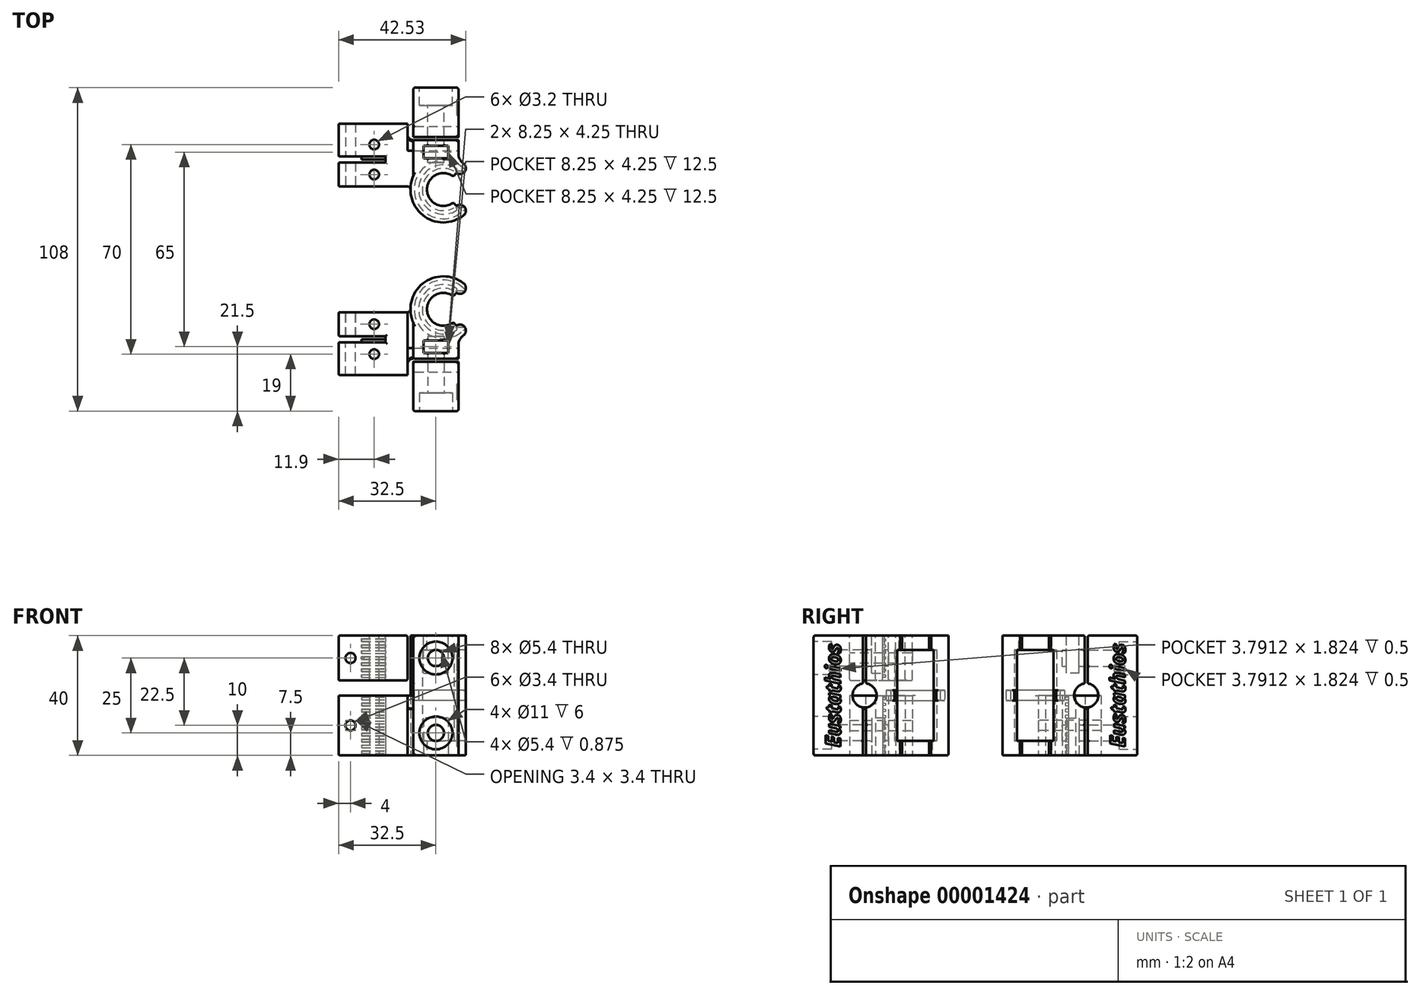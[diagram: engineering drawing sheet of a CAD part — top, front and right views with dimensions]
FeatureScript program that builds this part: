
annotation { "Feature Type Name" : "Feature", "Feature Type Description" : "" }
export const myFeature = defineFeature(function(context is Context, id is Id, definition is map)
    precondition{}
    {
        {
            var Q0;
            Q0=qCreatedBy(makeId("Top.planeOp"),FACE);
            var sketch = newSketch(context, id + "F0", { "sketchPlane" : qUnion([Q0])});
            skArc(sketch, "E0", {"start": v(5, -9.8) * mm, "mid": v(3.61, 10.39) * mm, "end": v(-10, -4.58) * mm});
            skLineSegment(sketch, "E1", {"start": v(5, -34) * mm, "end": v(5, -9.8) * mm});
            skLineSegment(sketch, "E2", {"start": v(-10, -4.58) * mm, "end": v(-10, -34) * mm});
            skLineSegment(sketch, "E3", {"start": v(-10, -34) * mm, "end": v(5, -34) * mm});
            skLineSegment(sketch, "E4", {"start": v(-10, -17) * mm, "end": v(5, -17) * mm, "construction": true});
            skSolve(sketch);
        }
        {
            var Q0;
            Q0 = qSketchRegion(id + "F0", true);
            extrude(context, id + "F1", {"entities" : qUnion([Q0]), "depth" : 40 * mm});
        }
        {
            var Q0;
            Q0=makeQuery(id+"F1.opExtrude","CAP_FACE",FACE,{"disambiguationData":[OSD([sQuery(id+"F0.wireOp",EDGE,"E0"),sQuery(id+"F0.wireOp",EDGE,"E1"),sQuery(id+"F0.wireOp",EDGE,"E2"),sQuery(id+"F0.wireOp",EDGE,"E3")])],"isStart":true});
            var Q1;
            Q1=makeQuery(id+"F1.opExtrude","CAP_FACE",FACE,{"disambiguationData":[OSD([sQuery(id+"F0.wireOp",EDGE,"E0"),sQuery(id+"F0.wireOp",EDGE,"E1"),sQuery(id+"F0.wireOp",EDGE,"E2"),sQuery(id+"F0.wireOp",EDGE,"E3")])],"isStart":false});
            cPlane(context, id + "F2", {"entities" : qUnion([Q0, Q1]), "cplaneType" : CPlaneType.MID_PLANE, "offset" : 150 * mm, "width" : 150 * mm, "height" : 150 * mm});
        }
        {
            var Q0;
            Q0=makeQuery(id+"F1.opExtrude","CAP_FACE",FACE,{"disambiguationData":[OSD([sQuery(id+"F0.wireOp",EDGE,"E0"),sQuery(id+"F0.wireOp",EDGE,"E1"),sQuery(id+"F0.wireOp",EDGE,"E2"),sQuery(id+"F0.wireOp",EDGE,"E3")])],"isStart":true});
            var sketch = newSketch(context, id + "F3", { "sketchPlane" : qUnion([Q0])});
            skLineSegment(sketch, "E5", {"start": v(-35, 1) * mm, "end": v(-35, 9) * mm});
            skLineSegment(sketch, "E6", {"start": v(-35, 9) * mm, "end": v(-19.3, 9) * mm});
            skLineSegment(sketch, "E7", {"start": v(-19.3, 9) * mm, "end": v(-19.3, 11) * mm});
            skLineSegment(sketch, "E8", {"start": v(-19.3, 11) * mm, "end": v(-35, 11) * mm});
            skLineSegment(sketch, "E9", {"start": v(-35, 11) * mm, "end": v(-35, 22) * mm});
            skLineSegment(sketch, "E10", {"start": v(-35, 22) * mm, "end": v(-10, 22) * mm});
            skLineSegment(sketch, "E11", {"start": v(-10, 22) * mm, "end": v(-10, 4.58) * mm});
            skArc(sketch, "E12", {"start": v(-10, 4.58) * mm, "mid": v(-10.75, 2.35) * mm, "end": v(-11, 0) * mm});
            skLineSegment(sketch, "E13", {"start": v(-35, 11) * mm, "end": v(-35, 9) * mm, "construction": true});
            skLineSegment(sketch, "E14", {"start": v(-35, 10) * mm, "end": v(-19.3, 10) * mm, "construction": true});
            skLineSegment(sketch, "E15", {"start": v(-35, 1) * mm, "end": v(-12, 1) * mm});
            skArc(sketch, "E16", {"start": v(-12, 1) * mm, "mid": v(-11.3, 0.7) * mm, "end": v(-11, 0) * mm});
            skSolve(sketch);
        }
        {
            var Q0;
            Q0 = qSketchRegion(id + "F3", true);
            var Q1;
            Q1=qCreatedBy(id+"F2.planeOp",FACE);
            extrude(context, id + "F4", {"entities" : qUnion([Q0]), "operationType" : NewBodyOperationType.ADD, "endBound" : BoundingType.UP_TO_SURFACE, "oppositeDirection" : true, "endBoundEntityFace" : qUnion([Q1]), "depth" : 21 * mm});
        }
        {
            var Q0;
            Q0=makeQuery(id+"F1.opExtrude","SWEPT_FACE",FACE,{"disambiguationData":[OSD([sQuery(id+"F0.wireOp",EDGE,"E1")])]});
            var sketch = newSketch(context, id + "F5", { "sketchPlane" : qUnion([Q0])});
            skLineSegment(sketch, "E17", {"start": v(0, 0) * mm, "end": v(0, 40) * mm, "construction": true});
            skLineSegment(sketch, "E18.0", {"start": v(-9.8, 40) * mm, "end": v(11, 40) * mm, "construction": true});
            skLineSegment(sketch, "E19", {"start": v(0, 20) * mm, "end": v(-17, 20) * mm, "construction": true});
            skPoint(sketch, "E19.endSnap0", {"position": v(0, 20) * mm});
            skLineSegment(sketch, "E20", {"start": v(-17, 20) * mm, "end": v(-34, 20) * mm, "construction": true});
            skCircle(sketch, "E21", {"center": v(-17, 20) * mm, "radius": 4.03 * mm});
            skSolve(sketch);
        }
        {
            var Q0;
            Q0 = qSketchRegion(id + "F5", true);
            var Q1;
            Q1=makeQuery(id+"F1.opExtrude","SWEPT_FACE",FACE,{"disambiguationData":[OSD([sQuery(id+"F0.wireOp",EDGE,"E2")])]});
            extrude(context, id + "F6", {"entities" : qUnion([Q0]), "operationType" : NewBodyOperationType.REMOVE, "oppositeDirection" : true, "endBoundEntityFace" : qUnion([Q1]), "depth" : 17 * mm});
        }
        {
            var Q0;
            Q0=makeQuery(id+"F4.boolean.opBoolean","MERGE",FACE,{"derivedFrom":[makeQuery(id+"F1.opExtrude","CAP_FACE",FACE,{"disambiguationData":[OSD([sQuery(id+"F0.wireOp",EDGE,"E0"),sQuery(id+"F0.wireOp",EDGE,"E1"),sQuery(id+"F0.wireOp",EDGE,"E2"),sQuery(id+"F0.wireOp",EDGE,"E3")])],"isStart":true}),makeQuery(id+"F4.opExtrude","CAP_FACE",FACE,{"disambiguationData":[OSD([sQuery(id+"F3.wireOp",EDGE,"E5"),sQuery(id+"F3.wireOp",EDGE,"E6"),sQuery(id+"F3.wireOp",EDGE,"E7"),sQuery(id+"F3.wireOp",EDGE,"E8"),sQuery(id+"F3.wireOp",EDGE,"E9"),sQuery(id+"F3.wireOp",EDGE,"E10"),sQuery(id+"F3.wireOp",EDGE,"E11"),sQuery(id+"F3.wireOp",EDGE,"E12"),sQuery(id+"F3.wireOp",EDGE,"E15"),sQuery(id+"F3.wireOp",EDGE,"E16")])],"isStart":true})]});
            var sketch = newSketch(context, id + "F7", { "sketchPlane" : qUnion([Q0])});
            skLineSegment(sketch, "E22.0", {"start": v(-12, 12.98) * mm, "end": v(-10, 12.98) * mm, "construction": true});
            skLineSegment(sketch, "E23.0", {"start": v(-12, 12.97) * mm, "end": v(-12, 12.97) * mm});
            skLineSegment(sketch, "E24", {"start": v(-10, 17.5) * mm, "end": v(5, 17.5) * mm});
            skLineSegment(sketch, "E25", {"start": v(5, 17.5) * mm, "end": v(5, 16.5) * mm});
            skLineSegment(sketch, "E26", {"start": v(5, 17) * mm, "end": v(-12, 17) * mm, "construction": true});
            skLineSegment(sketch, "E27", {"start": v(5, 16.5) * mm, "end": v(-10, 16.5) * mm});
            skLineSegment(sketch, "E28.0", {"start": v(-12, 12.97) * mm, "end": v(-12, 21.03) * mm, "construction": true});
            skLineSegment(sketch, "E29", {"start": v(-10, 22) * mm, "end": v(-10, 17.5) * mm});
            skLineSegment(sketch, "E30", {"start": v(-10, 22) * mm, "end": v(-12, 22) * mm});
            skLineSegment(sketch, "E31", {"start": v(-12, 22) * mm, "end": v(-12, 18.5) * mm});
            skPoint(sketch, "E32.visualSharp", {"position": v(-12, 16.5) * mm});
            skArc(sketch, "E32.filletArc", {"start": v(-12, 18.5) * mm, "mid": v(-11.41, 17.09) * mm, "end": v(-10, 16.5) * mm});
            skSolve(sketch);
        }
        {
            var Q0;
            Q0 = qSketchRegion(id + "F7", true);
            extrude(context, id + "F8", {"entities" : qUnion([Q0]), "operationType" : NewBodyOperationType.REMOVE, "endBound" : BoundingType.THROUGH_ALL, "oppositeDirection" : true, "depth" : 25 * mm});
        }
        {
            var Q0;
            {var subQ0=sQuery(id+"F3.wireOp",EDGE,"E10");var subQ1=sQuery(id+"F3.wireOp",EDGE,"E9");var subQ2=sQuery(id+"F3.wireOp",EDGE,"E8");var subQ3=sQuery(id+"F3.wireOp",EDGE,"E7");var subQ4=sQuery(id+"F0.wireOp",EDGE,"E1");var subQ5=sQuery(id+"F0.wireOp",EDGE,"E0");var subQ6=sQuery(id+"F3.wireOp",EDGE,"E16");var subQ7=sQuery(id+"F3.wireOp",EDGE,"E15");var subQ8=sQuery(id+"F3.wireOp",EDGE,"E5");var subQ9=sQuery(id+"F3.wireOp",EDGE,"E6");Q0=makeQuery(id+"F8.boolean.opBoolean","SPLIT",FACE,{"disambiguationData":[TD([makeQuery(id+"F1.opExtrude","SWEPT_FACE",FACE,{"disambiguationData":[OSD([subQ5])]})])],"derivedFrom":makeQuery(id+"F4.boolean.opBoolean","MERGE",FACE,{"derivedFrom":[makeQuery(id+"F1.opExtrude","CAP_FACE",FACE,{"disambiguationData":[OSD([subQ5,subQ4,sQuery(id+"F0.wireOp",EDGE,"E2"),sQuery(id+"F0.wireOp",EDGE,"E3")])],"isStart":true}),makeQuery(id+"F4.opExtrude","CAP_FACE",FACE,{"disambiguationData":[OSD([subQ8,subQ9,subQ3,subQ2,subQ1,subQ0,sQuery(id+"F3.wireOp",EDGE,"E11"),sQuery(id+"F3.wireOp",EDGE,"E12"),subQ7,subQ6])],"isStart":true})]})});}
            var sketch = newSketch(context, id + "F9", { "sketchPlane" : qUnion([Q0])});
            skCircle(sketch, "E33", {"center": v(0, 0) * mm, "radius": 7.05 * mm});
            skSolve(sketch);
        }
        {
            var Q0;
            Q0 = qSketchRegion(id + "F9", true);
            extrude(context, id + "F10", {"entities" : qUnion([Q0]), "operationType" : NewBodyOperationType.REMOVE, "endBound" : BoundingType.THROUGH_ALL, "oppositeDirection" : true, "depth" : 25 * mm});
        }
        {
            var Q0;
            {var subQ0=sQuery(id+"F3.wireOp",EDGE,"E10");var subQ1=sQuery(id+"F3.wireOp",EDGE,"E9");var subQ2=sQuery(id+"F3.wireOp",EDGE,"E8");var subQ3=sQuery(id+"F3.wireOp",EDGE,"E7");var subQ4=sQuery(id+"F0.wireOp",EDGE,"E1");var subQ5=sQuery(id+"F0.wireOp",EDGE,"E0");var subQ6=sQuery(id+"F3.wireOp",EDGE,"E16");var subQ7=sQuery(id+"F3.wireOp",EDGE,"E15");var subQ8=sQuery(id+"F3.wireOp",EDGE,"E5");var subQ9=sQuery(id+"F3.wireOp",EDGE,"E6");Q0=makeQuery(id+"F8.boolean.opBoolean","SPLIT",FACE,{"disambiguationData":[TD([makeQuery(id+"F1.opExtrude","SWEPT_FACE",FACE,{"disambiguationData":[OSD([subQ5])]})])],"derivedFrom":makeQuery(id+"F4.boolean.opBoolean","MERGE",FACE,{"derivedFrom":[makeQuery(id+"F1.opExtrude","CAP_FACE",FACE,{"disambiguationData":[OSD([subQ5,subQ4,sQuery(id+"F0.wireOp",EDGE,"E2"),sQuery(id+"F0.wireOp",EDGE,"E3")])],"isStart":true}),makeQuery(id+"F4.opExtrude","CAP_FACE",FACE,{"disambiguationData":[OSD([subQ8,subQ9,subQ3,subQ2,subQ1,subQ0,sQuery(id+"F3.wireOp",EDGE,"E11"),sQuery(id+"F3.wireOp",EDGE,"E12"),subQ7,subQ6])],"isStart":true})]})});}
            var sketch = newSketch(context, id + "F11", { "sketchPlane" : qUnion([Q0])});
            skLineSegment(sketch, "E34", {"start": v(0, 0) * mm, "end": v(8.5, 6.98) * mm, "construction": true});
            skLineSegment(sketch, "E35", {"start": v(8.5, -6.98) * mm, "end": v(0, 0) * mm, "construction": true});
            skArc(sketch, "E36", {"start": v(6.77, -8.67) * mm, "mid": v(7.11, -5.9) * mm, "end": v(4.34, -5.56) * mm});
            skLineSegment(sketch, "E37", {"start": v(0, 0) * mm, "end": v(14.65, 0) * mm, "construction": true});
            skArc(sketch, "E38", {"start": v(4.34, 5.56) * mm, "mid": v(7.11, 5.9) * mm, "end": v(6.77, 8.67) * mm});
            skLineSegment(sketch, "E39", {"start": v(5.56, 7.11) * mm, "end": v(0, 0) * mm, "construction": true});
            skLineSegment(sketch, "E40", {"start": v(0, 0) * mm, "end": v(5.56, -7.11) * mm, "construction": true});
            skArc(sketch, "E41", {"start": v(4.34, 5.56) * mm, "mid": v(7.05, 0) * mm, "end": v(4.34, -5.56) * mm});
            skSolve(sketch);
        }
        {
            var Q0;
            Q0 = qSketchRegion(id + "F11", true);
            var Q1;
            {var subQ2=sQuery(id+"F11.wireOp",EDGE,"E36");Q1=makeQuery(id+"F11.imprint","IMPRINT",FACE,{"disambiguationData":[TD([[makeQuery(id+"F11.imprint","IMPRINT",EDGE,{"derivedFrom":subQ2}),-1.0]])]});}
            extrude(context, id + "F12", {"entities" : qUnion([Q0, Q1]), "operationType" : NewBodyOperationType.REMOVE, "endBound" : BoundingType.THROUGH_ALL, "oppositeDirection" : true, "depth" : 25 * mm});
        }
        {
            var Q0;
            Q0=makeQuery(id+"F1.opExtrude","SWEPT_EDGE",EDGE,{"disambiguationData":[OSD([sQuery(id+"F0.wireOp",EDGE,"E0"),sQuery(id+"F0.wireOp",EDGE,"E1")])]});
            fillet(context, id + "F13", {"entities" : qUnion([Q0]), "radius" : 4 * mm, "tangentPropagation" : true, "allowEdgeOverflow" : false});
        }
        {
            var Q0;
            Q0=qCreatedBy(makeId("Right.planeOp"),FACE);
            var sketch = newSketch(context, id + "F14", { "sketchPlane" : qUnion([Q0])});
            skLineSegment(sketch, "E42.rect.bottom", {"start": v(-6.1, 35.2) * mm, "end": v(6.1, 35.2) * mm});
            skLineSegment(sketch, "E42.rect.top", {"start": v(-6.1, 4.8) * mm, "end": v(6.1, 4.8) * mm});
            skLineSegment(sketch, "E42.rect.left", {"start": v(-6.1, 35.2) * mm, "end": v(-6.1, 4.8) * mm});
            skLineSegment(sketch, "E42.rect.right", {"start": v(6.1, 35.2) * mm, "end": v(6.1, 4.8) * mm});
            skPoint(sketch, "E42.rect.middle", {"position": v(0, 20) * mm});
            skLineSegment(sketch, "E43", {"start": v(-5.14, 40) * mm, "end": v(-5.14, 0) * mm, "construction": true});
            skLineSegment(sketch, "E44", {"start": v(5.14, 0) * mm, "end": v(5.14, 40) * mm, "construction": true});
            skLineSegment(sketch, "E45", {"start": v(-5.14, 0) * mm, "end": v(5.14, 0) * mm, "construction": true});
            skLineSegment(sketch, "E46", {"start": v(-5.14, 40) * mm, "end": v(5.14, 40) * mm, "construction": true});
            skLineSegment(sketch, "E47", {"start": v(0, 0) * mm, "end": v(0, 40) * mm, "construction": true});
            skSolve(sketch);
        }
        {
            var Q0;
            Q0 = qSketchRegion(id + "F14", true);
            extrude(context, id + "F15", {"entities" : qUnion([Q0]), "operationType" : NewBodyOperationType.REMOVE, "endBound" : BoundingType.THROUGH_ALL, "depth" : 25 * mm});
        }
        {
            var Q0;
            {var subQ0=sQuery(id+"F3.wireOp",EDGE,"E10");var subQ1=sQuery(id+"F3.wireOp",EDGE,"E9");var subQ2=sQuery(id+"F3.wireOp",EDGE,"E8");var subQ3=sQuery(id+"F3.wireOp",EDGE,"E7");var subQ4=sQuery(id+"F0.wireOp",EDGE,"E1");var subQ5=sQuery(id+"F0.wireOp",EDGE,"E0");var subQ6=sQuery(id+"F3.wireOp",EDGE,"E16");var subQ7=sQuery(id+"F3.wireOp",EDGE,"E15");var subQ8=sQuery(id+"F3.wireOp",EDGE,"E5");var subQ9=sQuery(id+"F3.wireOp",EDGE,"E6");Q0=makeQuery(id+"F8.boolean.opBoolean","SPLIT",FACE,{"disambiguationData":[TD([makeQuery(id+"F1.opExtrude","SWEPT_FACE",FACE,{"disambiguationData":[OSD([subQ5])]})])],"derivedFrom":makeQuery(id+"F4.boolean.opBoolean","MERGE",FACE,{"derivedFrom":[makeQuery(id+"F1.opExtrude","CAP_FACE",FACE,{"disambiguationData":[OSD([subQ5,subQ4,sQuery(id+"F0.wireOp",EDGE,"E2"),sQuery(id+"F0.wireOp",EDGE,"E3")])],"isStart":true}),makeQuery(id+"F4.opExtrude","CAP_FACE",FACE,{"disambiguationData":[OSD([subQ8,subQ9,subQ3,subQ2,subQ1,subQ0,sQuery(id+"F3.wireOp",EDGE,"E11"),sQuery(id+"F3.wireOp",EDGE,"E12"),subQ7,subQ6])],"isStart":true})]})});}
            var sketch = newSketch(context, id + "F16", { "sketchPlane" : qUnion([Q0])});
            skArc(sketch, "E48", {"start": v(3.39, 4.33) * mm, "mid": v(-5.5, 0) * mm, "end": v(3.39, -4.33) * mm});
            skArc(sketch, "E49.0", {"start": v(4.34, 5.56) * mm, "mid": v(-7.05, 0) * mm, "end": v(4.34, -5.56) * mm});
            skLineSegment(sketch, "E50", {"start": v(0, 0) * mm, "end": v(6.8, 5.58) * mm, "construction": true});
            skLineSegment(sketch, "E51", {"start": v(0, 0) * mm, "end": v(6.8, -5.58) * mm, "construction": true});
            skArc(sketch, "E52", {"start": v(4.34, 5.56) * mm, "mid": v(5.58, 5.14) * mm, "end": v(6.8, 5.58) * mm});
            skArc(sketch, "E53", {"start": v(4.34, -5.56) * mm, "mid": v(5.58, -5.14) * mm, "end": v(6.8, -5.58) * mm});
            skLineSegment(sketch, "E54", {"start": v(4.34, 5.56) * mm, "end": v(3.39, 4.33) * mm});
            skLineSegment(sketch, "E55", {"start": v(3.39, -4.33) * mm, "end": v(4.34, -5.56) * mm});
            skLineSegment(sketch, "E56", {"start": v(3.39, 4.33) * mm, "end": v(0, 0) * mm, "construction": true});
            skLineSegment(sketch, "E57", {"start": v(3.39, -4.33) * mm, "end": v(0, 0) * mm, "construction": true});
            skSolve(sketch);
        }
        {
            var Q0;
            Q0 = qSketchRegion(id + "F16", true);
            var Q1;
            Q1=makeQuery(id+"F15.boolean.opBoolean","COPY",FACE,{"disambiguationData":[OD(0.0)],"derivedFrom":makeQuery(id+"F15.opExtrude","SWEPT_FACE",FACE,{"disambiguationData":[OSD([sQuery(id+"F14.wireOp",EDGE,"E42.rect.top")])]})});
            extrude(context, id + "F17", {"entities" : qUnion([Q0]), "operationType" : NewBodyOperationType.ADD, "endBound" : BoundingType.UP_TO_SURFACE, "oppositeDirection" : true, "endBoundEntityFace" : qUnion([Q1]), "depth" : 2.4 * mm});
        }
        {
            var Q0;
            {var subQ0=sQuery(id+"F0.wireOp",EDGE,"E0");var subQ1=sQuery(id+"F0.wireOp",EDGE,"E1");var subQ2=sQuery(id+"F0.wireOp",EDGE,"E2");Q0=makeQuery(id+"F8.boolean.opBoolean","SPLIT",FACE,{"disambiguationData":[TD([makeQuery(id+"F1.opExtrude","SWEPT_FACE",FACE,{"disambiguationData":[OSD([subQ0])]})])],"derivedFrom":makeQuery(id+"F1.opExtrude","CAP_FACE",FACE,{"disambiguationData":[OSD([subQ0,subQ1,subQ2,sQuery(id+"F0.wireOp",EDGE,"E3")])],"isStart":false})});}
            var sketch = newSketch(context, id + "F18", { "sketchPlane" : qUnion([Q0])});
            skArc(sketch, "E58.0", {"start": v(3.39, -4.33) * mm, "mid": v(-5.5, 0) * mm, "end": v(3.39, 4.33) * mm});
            skLineSegment(sketch, "E59.0", {"start": v(4.34, -5.56) * mm, "end": v(3.39, -4.33) * mm});
            skLineSegment(sketch, "E60.0", {"start": v(3.39, 4.33) * mm, "end": v(4.34, 5.56) * mm});
            skArc(sketch, "E61.0", {"start": v(4.34, 5.56) * mm, "mid": v(-7.05, 0) * mm, "end": v(4.34, -5.56) * mm});
            skSolve(sketch);
        }
        {
            var Q0;
            Q0 = qSketchRegion(id + "F18", true);
            var Q1;
            Q1=makeQuery(id+"F15.boolean.opBoolean","COPY",FACE,{"disambiguationData":[OD(0.0)],"derivedFrom":makeQuery(id+"F15.opExtrude","SWEPT_FACE",FACE,{"disambiguationData":[OSD([sQuery(id+"F14.wireOp",EDGE,"E42.rect.bottom")])]})});
            extrude(context, id + "F19", {"entities" : qUnion([Q0]), "operationType" : NewBodyOperationType.ADD, "endBound" : BoundingType.UP_TO_SURFACE, "oppositeDirection" : true, "endBoundEntityFace" : qUnion([Q1]), "depth" : 2.4 * mm});
        }
        {
            var Q0;
            {var subQ0=sQuery(id+"F0.wireOp",EDGE,"E0");var subQ1=sQuery(id+"F0.wireOp",EDGE,"E1");var subQ2=sQuery(id+"F0.wireOp",EDGE,"E2");Q0=makeQuery(id+"F19.boolean.opBoolean","MERGE",FACE,{"derivedFrom":[makeQuery(id+"F8.boolean.opBoolean","SPLIT",FACE,{"disambiguationData":[TD([makeQuery(id+"F1.opExtrude","SWEPT_FACE",FACE,{"disambiguationData":[OSD([subQ0])]})])],"derivedFrom":makeQuery(id+"F1.opExtrude","CAP_FACE",FACE,{"disambiguationData":[OSD([subQ0,subQ1,subQ2,sQuery(id+"F0.wireOp",EDGE,"E3")])],"isStart":false})}),makeQuery(id+"F19.opExtrude","CAP_FACE",FACE,{"disambiguationData":[OSD([sQuery(id+"F18.wireOp",EDGE,"825981b6-10bd-436c-b23c-b1dcfb23399f.0"),sQuery(id+"F18.wireOp",EDGE,"26848335-8289-480a-91f7-f3094b967ab5.0"),sQuery(id+"F18.wireOp",EDGE,"958e6e3c-ce8c-4eca-b8df-495d4845233b.0"),sQuery(id+"F18.wireOp",EDGE,"a21f0ce2-bef5-4404-b2f3-7f19712db0ed.0"),sQuery(id+"F18.wireOp",EDGE,"5b232a10-1d2d-4218-a2a3-206db68530f9.0"),sQuery(id+"F18.wireOp",EDGE,"9355f6d4-eb2a-417f-8d43-74a68f565168.0")])],"isStart":true})]});}
            var sketch = newSketch(context, id + "F20", { "sketchPlane" : qUnion([Q0])});
            skLineSegment(sketch, "E62", {"start": v(-2.5, -16.5) * mm, "end": v(-2.5, -12.5) * mm, "construction": true});
            skLineSegment(sketch, "E63.rect.bottom", {"start": v(-6.62, -14.62) * mm, "end": v(1.63, -14.62) * mm});
            skLineSegment(sketch, "E63.rect.top", {"start": v(-6.62, -10.37) * mm, "end": v(1.63, -10.38) * mm});
            skLineSegment(sketch, "E63.rect.left", {"start": v(-6.62, -14.62) * mm, "end": v(-6.62, -10.37) * mm});
            skLineSegment(sketch, "E63.rect.right", {"start": v(1.63, -14.62) * mm, "end": v(1.63, -10.38) * mm});
            skPoint(sketch, "E63.rect.middle", {"position": v(-2.5, -12.5) * mm});
            skSolve(sketch);
        }
        {
            var Q0;
            Q0 = qSketchRegion(id + "F20", true);
            extrude(context, id + "F21", {"entities" : qUnion([Q0]), "operationType" : NewBodyOperationType.REMOVE, "oppositeDirection" : true, "depth" : 12.5 * mm});
        }
        {
            var Q0;
            {var subQ0=sQuery(id+"F3.wireOp",EDGE,"E10");var subQ1=sQuery(id+"F3.wireOp",EDGE,"E9");var subQ2=sQuery(id+"F3.wireOp",EDGE,"E8");var subQ3=sQuery(id+"F3.wireOp",EDGE,"E7");var subQ4=sQuery(id+"F0.wireOp",EDGE,"E1");var subQ5=sQuery(id+"F0.wireOp",EDGE,"E0");var subQ6=sQuery(id+"F3.wireOp",EDGE,"E16");var subQ7=sQuery(id+"F3.wireOp",EDGE,"E15");var subQ8=sQuery(id+"F3.wireOp",EDGE,"E5");var subQ9=sQuery(id+"F3.wireOp",EDGE,"E6");Q0=makeQuery(id+"F17.boolean.opBoolean","MERGE",FACE,{"derivedFrom":[makeQuery(id+"F8.boolean.opBoolean","SPLIT",FACE,{"disambiguationData":[TD([makeQuery(id+"F1.opExtrude","SWEPT_FACE",FACE,{"disambiguationData":[OSD([subQ5])]})])],"derivedFrom":makeQuery(id+"F4.boolean.opBoolean","MERGE",FACE,{"derivedFrom":[makeQuery(id+"F1.opExtrude","CAP_FACE",FACE,{"disambiguationData":[OSD([subQ5,subQ4,sQuery(id+"F0.wireOp",EDGE,"E2"),sQuery(id+"F0.wireOp",EDGE,"E3")])],"isStart":true}),makeQuery(id+"F4.opExtrude","CAP_FACE",FACE,{"disambiguationData":[OSD([subQ8,subQ9,subQ3,subQ2,subQ1,subQ0,sQuery(id+"F3.wireOp",EDGE,"E11"),sQuery(id+"F3.wireOp",EDGE,"E12"),subQ7,subQ6])],"isStart":true})]})}),makeQuery(id+"F17.opExtrude","CAP_FACE",FACE,{"disambiguationData":[OSD([sQuery(id+"F16.wireOp",EDGE,"E48"),sQuery(id+"F16.wireOp",EDGE,"E49.0"),sQuery(id+"F16.wireOp",EDGE,"E54"),sQuery(id+"F16.wireOp",EDGE,"E55")])],"isStart":true})]});}
            var sketch = newSketch(context, id + "F22", { "sketchPlane" : qUnion([Q0])});
            skLineSegment(sketch, "E64.0.0", {"start": v(-6.62, 10.37) * mm, "end": v(-6.62, 14.62) * mm});
            skLineSegment(sketch, "E64.0.1", {"start": v(-6.62, 14.62) * mm, "end": v(1.63, 14.62) * mm});
            skLineSegment(sketch, "E64.0.2", {"start": v(1.63, 14.62) * mm, "end": v(1.63, 10.38) * mm});
            skLineSegment(sketch, "E64.0.3", {"start": v(1.63, 10.38) * mm, "end": v(-6.62, 10.37) * mm});
            skSolve(sketch);
        }
        {
            var Q0;
            Q0 = qSketchRegion(id + "F22", true);
            extrude(context, id + "F23", {"entities" : qUnion([Q0]), "operationType" : NewBodyOperationType.REMOVE, "oppositeDirection" : true, "depth" : 12.5 * mm});
        }
        {
            var Q0;
            Q0=makeQuery(id+"F1.opExtrude","SWEPT_FACE",FACE,{"disambiguationData":[OSD([sQuery(id+"F0.wireOp",EDGE,"E3")])]});
            var sketch = newSketch(context, id + "F24", { "sketchPlane" : qUnion([Q0])});
            skLineSegment(sketch, "E65", {"start": v(-2.5, 0) * mm, "end": v(-2.5, 7.5) * mm, "construction": true});
            skLineSegment(sketch, "E66", {"start": v(-2.5, 7.5) * mm, "end": v(-2.5, 32.5) * mm, "construction": true});
            skLineSegment(sketch, "E67", {"start": v(-2.5, 32.5) * mm, "end": v(-2.5, 40) * mm, "construction": true});
            skLineSegment(sketch, "E68", {"start": v(-2.5, 7.5) * mm, "end": v(-10, 7.5) * mm, "construction": true});
            skLineSegment(sketch, "E69", {"start": v(-2.5, 32.5) * mm, "end": v(-10, 32.5) * mm, "construction": true});
            skCircle(sketch, "E70", {"center": v(-2.5, 7.5) * mm, "radius": 2.7 * mm});
            skCircle(sketch, "E71", {"center": v(-2.5, 32.5) * mm, "radius": 2.7 * mm});
            skSolve(sketch);
        }
        {
            var Q0;
            Q0 = qSketchRegion(id + "F24", true);
            extrude(context, id + "F25", {"entities" : qUnion([Q0]), "operationType" : NewBodyOperationType.REMOVE, "oppositeDirection" : true, "depth" : 25 * mm});
        }
        {
            var Q0;
            Q0=makeQuery(id+"F1.opExtrude","SWEPT_FACE",FACE,{"disambiguationData":[OSD([sQuery(id+"F0.wireOp",EDGE,"E3")])]});
            var sketch = newSketch(context, id + "F26", { "sketchPlane" : qUnion([Q0])});
            skCircle(sketch, "E72", {"center": v(-2.5, 32.5) * mm, "radius": 5.5 * mm});
            skCircle(sketch, "E73", {"center": v(-2.5, 7.5) * mm, "radius": 5.5 * mm});
            skSolve(sketch);
        }
        {
            var Q0;
            Q0 = qSketchRegion(id + "F26", true);
            extrude(context, id + "F27", {"entities" : qUnion([Q0]), "operationType" : NewBodyOperationType.REMOVE, "oppositeDirection" : true, "depth" : 6 * mm});
        }
        {
            var Q0;
            Q0=makeQuery(id+"F8.boolean.opBoolean","INTERSECT",EDGE,{"derivedFrom":[makeQuery(id+"F6.boolean.opBoolean","COPY",FACE,{"derivedFrom":makeQuery(id+"F6.opExtrude","SWEPT_FACE",FACE,{"disambiguationData":[OSD([sQuery(id+"F5.wireOp",EDGE,"E21")])]})}),makeQuery(id+"F8.opExtrude","SWEPT_FACE",FACE,{"disambiguationData":[OSD([sQuery(id+"F7.wireOp",EDGE,"E29")])]})]});
            var Q1;
            Q1=makeQuery(id+"F8.boolean.opBoolean","INTERSECT",EDGE,{"disambiguationData":[OD(0.0)],"derivedFrom":[makeQuery(id+"F6.boolean.opBoolean","COPY",FACE,{"derivedFrom":makeQuery(id+"F6.opExtrude","SWEPT_FACE",FACE,{"disambiguationData":[OSD([sQuery(id+"F5.wireOp",EDGE,"E21")])]})}),makeQuery(id+"F8.opExtrude","SWEPT_FACE",FACE,{"disambiguationData":[OSD([sQuery(id+"F7.wireOp",EDGE,"E24")])]})]});
            var Q2;
            Q2=makeQuery(id+"F8.boolean.opBoolean","INTERSECT",EDGE,{"disambiguationData":[OD(1.0)],"derivedFrom":[makeQuery(id+"F6.boolean.opBoolean","COPY",FACE,{"derivedFrom":makeQuery(id+"F6.opExtrude","SWEPT_FACE",FACE,{"disambiguationData":[OSD([sQuery(id+"F5.wireOp",EDGE,"E21")])]})}),makeQuery(id+"F8.opExtrude","SWEPT_FACE",FACE,{"disambiguationData":[OSD([sQuery(id+"F7.wireOp",EDGE,"E24")])]})]});
            var Q3;
            Q3=makeQuery(id+"F8.boolean.opBoolean","COPY",EDGE,{"disambiguationData":[OD(0.0)],"derivedFrom":makeQuery(id+"F8.opExtrude","SWEPT_EDGE",EDGE,{"disambiguationData":[OSD([sQuery(id+"F7.wireOp",EDGE,"E24"),sQuery(id+"F7.wireOp",EDGE,"E29")])]})});
            var Q4;
            Q4=makeQuery(id+"F8.boolean.opBoolean","COPY",EDGE,{"disambiguationData":[OD(1.0)],"derivedFrom":makeQuery(id+"F8.opExtrude","SWEPT_EDGE",EDGE,{"disambiguationData":[OSD([sQuery(id+"F7.wireOp",EDGE,"E24"),sQuery(id+"F7.wireOp",EDGE,"E29")])]})});
            var Q5;
            Q5=makeQuery(id+"F8.boolean.opBoolean","INTERSECT",EDGE,{"derivedFrom":[makeQuery(id+"F1.opExtrude","CAP_FACE",FACE,{"disambiguationData":[OSD([sQuery(id+"F0.wireOp",EDGE,"E0"),sQuery(id+"F0.wireOp",EDGE,"E1"),sQuery(id+"F0.wireOp",EDGE,"E2"),sQuery(id+"F0.wireOp",EDGE,"E3")])],"isStart":false}),makeQuery(id+"F8.opExtrude","SWEPT_FACE",FACE,{"disambiguationData":[OSD([sQuery(id+"F7.wireOp",EDGE,"E24")])]})]});
            var Q6;
            {var subQ0=sQuery(id+"F0.wireOp",EDGE,"E2");var subQ1=sQuery(id+"F0.wireOp",EDGE,"E3");Q6=makeQuery(id+"F8.boolean.opBoolean","SPLIT",EDGE,{"disambiguationData":[TD([makeQuery(id+"F1.opExtrude","SWEPT_FACE",FACE,{"disambiguationData":[OSD([subQ1])]})])],"derivedFrom":makeQuery(id+"F1.opExtrude","CAP_EDGE",EDGE,{"disambiguationData":[OSD([subQ0])],"isStart":false})});}
            var Q7;
            Q7=makeQuery(id+"F1.opExtrude","CAP_EDGE",EDGE,{"disambiguationData":[OSD([sQuery(id+"F0.wireOp",EDGE,"E3")])],"isStart":false});
            var Q8;
            {var subQ0=sQuery(id+"F0.wireOp",EDGE,"E1");var subQ1=sQuery(id+"F0.wireOp",EDGE,"E3");Q8=makeQuery(id+"F8.boolean.opBoolean","SPLIT",EDGE,{"disambiguationData":[TD([makeQuery(id+"F1.opExtrude","SWEPT_FACE",FACE,{"disambiguationData":[OSD([subQ1])]})])],"derivedFrom":makeQuery(id+"F1.opExtrude","CAP_EDGE",EDGE,{"disambiguationData":[OSD([subQ0])],"isStart":false})});}
            var Q9;
            Q9=makeQuery(id+"F1.opExtrude","SWEPT_EDGE",EDGE,{"disambiguationData":[OSD([sQuery(id+"F0.wireOp",EDGE,"E2"),sQuery(id+"F0.wireOp",EDGE,"E3")])]});
            var Q10;
            Q10=makeQuery(id+"F1.opExtrude","SWEPT_EDGE",EDGE,{"disambiguationData":[OSD([sQuery(id+"F0.wireOp",EDGE,"E1"),sQuery(id+"F0.wireOp",EDGE,"E3")])]});
            var Q11;
            Q11=makeQuery(id+"F1.opExtrude","CAP_EDGE",EDGE,{"disambiguationData":[OSD([sQuery(id+"F0.wireOp",EDGE,"E3")])],"isStart":true});
            var Q12;
            Q12=makeQuery(id+"F8.boolean.opBoolean","COPY",EDGE,{"disambiguationData":[OD(1.0)],"derivedFrom":makeQuery(id+"F8.opExtrude","SWEPT_EDGE",EDGE,{"disambiguationData":[OSD([sQuery(id+"F0.wireOp",EDGE,"E1"),sQuery(id+"F7.wireOp",EDGE,"E24"),sQuery(id+"F7.wireOp",EDGE,"E25")])]})});
            var Q13;
            Q13=makeQuery(id+"F8.boolean.opBoolean","INTERSECT",EDGE,{"disambiguationData":[OD(1.0)],"derivedFrom":[makeQuery(id+"F6.boolean.opBoolean","COPY",FACE,{"derivedFrom":makeQuery(id+"F6.opExtrude","SWEPT_FACE",FACE,{"disambiguationData":[OSD([sQuery(id+"F5.wireOp",EDGE,"E21")])]})}),makeQuery(id+"F8.opExtrude","SWEPT_FACE",FACE,{"disambiguationData":[OSD([sQuery(id+"F7.wireOp",EDGE,"E24")])]})]});
            var Q14;
            Q14=makeQuery(id+"F8.boolean.opBoolean","COPY",EDGE,{"disambiguationData":[OD(0.0)],"derivedFrom":makeQuery(id+"F8.opExtrude","SWEPT_EDGE",EDGE,{"disambiguationData":[OSD([sQuery(id+"F0.wireOp",EDGE,"E1"),sQuery(id+"F7.wireOp",EDGE,"E24"),sQuery(id+"F7.wireOp",EDGE,"E25")])]})});
            var Q15;
            Q15=makeQuery(id+"F8.boolean.opBoolean","COPY",EDGE,{"derivedFrom":makeQuery(id+"F8.opExtrude","CAP_EDGE",EDGE,{"disambiguationData":[OSD([sQuery(id+"F7.wireOp",EDGE,"E24")])],"isStart":true})});
            var Q16;
            {var subQ0=sQuery(id+"F0.wireOp",EDGE,"E1");var subQ1=sQuery(id+"F0.wireOp",EDGE,"E3");Q16=makeQuery(id+"F8.boolean.opBoolean","SPLIT",EDGE,{"disambiguationData":[TD([makeQuery(id+"F1.opExtrude","SWEPT_FACE",FACE,{"disambiguationData":[OSD([subQ1])]})])],"derivedFrom":makeQuery(id+"F1.opExtrude","CAP_EDGE",EDGE,{"disambiguationData":[OSD([subQ0])],"isStart":true})});}
            var Q17;
            Q17=makeQuery(id+"F8.boolean.opBoolean","MERGE",EDGE,{"derivedFrom":[makeQuery(id+"F1.opExtrude","CAP_EDGE",EDGE,{"disambiguationData":[OSD([sQuery(id+"F0.wireOp",EDGE,"E2")])],"isStart":true}),makeQuery(id+"F8.opExtrude","CAP_EDGE",EDGE,{"disambiguationData":[OSD([sQuery(id+"F7.wireOp",EDGE,"E29")])],"isStart":true})]});
            var Q18;
            Q18=makeQuery(id+"F8.boolean.opBoolean","INTERSECT",EDGE,{"disambiguationData":[OD(0.0)],"derivedFrom":[makeQuery(id+"F6.boolean.opBoolean","COPY",FACE,{"derivedFrom":makeQuery(id+"F6.opExtrude","SWEPT_FACE",FACE,{"disambiguationData":[OSD([sQuery(id+"F5.wireOp",EDGE,"E21")])]})}),makeQuery(id+"F8.opExtrude","SWEPT_FACE",FACE,{"disambiguationData":[OSD([sQuery(id+"F7.wireOp",EDGE,"E24")])]})]});
            var Q19;
            {var subQ0=sQuery(id+"F5.wireOp",EDGE,"E21");Q19=makeQuery(id+"F8.boolean.opBoolean","SPLIT",EDGE,{"disambiguationData":[TD([makeQuery(id+"F8.opExtrude","SWEPT_FACE",FACE,{"disambiguationData":[OSD([sQuery(id+"F7.wireOp",EDGE,"E24")])]})])],"derivedFrom":makeQuery(id+"F6.boolean.opBoolean","COPY",EDGE,{"derivedFrom":makeQuery(id+"F6.opExtrude","CAP_EDGE",EDGE,{"disambiguationData":[OSD([subQ0])],"isStart":true})})});}
            var Q20;
            Q20=makeQuery(id+"F27.boolean.opBoolean","COPY",EDGE,{"derivedFrom":makeQuery(id+"F27.opExtrude","CAP_EDGE",EDGE,{"disambiguationData":[OSD([sQuery(id+"F26.wireOp",EDGE,"E73")])],"isStart":true})});
            var Q21;
            Q21=makeQuery(id+"F27.boolean.opBoolean","COPY",EDGE,{"derivedFrom":makeQuery(id+"F27.opExtrude","CAP_EDGE",EDGE,{"disambiguationData":[OSD([sQuery(id+"F26.wireOp",EDGE,"E72")])],"isStart":true})});
            var Q22;
            Q22=makeQuery(id+"F27.boolean.opBoolean","INTERSECT",EDGE,{"derivedFrom":[makeQuery(id+"F25.boolean.opBoolean","COPY",FACE,{"disambiguationData":[OD(0.0)],"derivedFrom":makeQuery(id+"F25.opExtrude","SWEPT_FACE",FACE,{"disambiguationData":[OSD([sQuery(id+"F24.wireOp",EDGE,"E70")])]})}),makeQuery(id+"F27.opExtrude","CAP_FACE",FACE,{"disambiguationData":[OSD([sQuery(id+"F26.wireOp",EDGE,"E73")])],"isStart":false})]});
            var Q23;
            Q23=makeQuery(id+"F27.boolean.opBoolean","INTERSECT",EDGE,{"derivedFrom":[makeQuery(id+"F25.boolean.opBoolean","COPY",FACE,{"disambiguationData":[OD(0.0)],"derivedFrom":makeQuery(id+"F25.opExtrude","SWEPT_FACE",FACE,{"disambiguationData":[OSD([sQuery(id+"F24.wireOp",EDGE,"E71")])]})}),makeQuery(id+"F27.opExtrude","CAP_FACE",FACE,{"disambiguationData":[OSD([sQuery(id+"F26.wireOp",EDGE,"E72")])],"isStart":false})]});
            var Q24;
            Q24=makeQuery(id+"F25.boolean.opBoolean","INTERSECT",EDGE,{"derivedFrom":[makeQuery(id+"F8.boolean.opBoolean","COPY",FACE,{"disambiguationData":[OD(1.0)],"derivedFrom":makeQuery(id+"F8.opExtrude","SWEPT_FACE",FACE,{"disambiguationData":[OSD([sQuery(id+"F7.wireOp",EDGE,"E24")])]})}),makeQuery(id+"F25.opExtrude","SWEPT_FACE",FACE,{"disambiguationData":[OSD([sQuery(id+"F24.wireOp",EDGE,"E71")])]})]});
            var Q25;
            Q25=makeQuery(id+"F25.boolean.opBoolean","INTERSECT",EDGE,{"derivedFrom":[makeQuery(id+"F8.boolean.opBoolean","COPY",FACE,{"disambiguationData":[OD(0.0)],"derivedFrom":makeQuery(id+"F8.opExtrude","SWEPT_FACE",FACE,{"disambiguationData":[OSD([sQuery(id+"F7.wireOp",EDGE,"E24")])]})}),makeQuery(id+"F25.opExtrude","SWEPT_FACE",FACE,{"disambiguationData":[OSD([sQuery(id+"F24.wireOp",EDGE,"E70")])]})]});
            fillet(context, id + "F28", {"entities" : qUnion([Q0, Q1, Q2, Q3, Q4, Q5, Q6, Q7, Q8, Q9, Q10, Q11, Q12, Q13, Q14, Q15, Q16, Q17, Q18, Q19, Q20, Q21, Q22, Q23, Q24, Q25]), "radius" : .5 * mm, "tangentPropagation" : true, "allowEdgeOverflow" : false});
        }
        {
            var Q0;
            {var subQ0=sQuery(id+"F3.wireOp",EDGE,"E10");var subQ1=sQuery(id+"F3.wireOp",EDGE,"E9");var subQ2=sQuery(id+"F3.wireOp",EDGE,"E8");var subQ3=sQuery(id+"F3.wireOp",EDGE,"E7");var subQ4=sQuery(id+"F0.wireOp",EDGE,"E1");var subQ5=sQuery(id+"F0.wireOp",EDGE,"E0");var subQ6=sQuery(id+"F3.wireOp",EDGE,"E16");var subQ7=sQuery(id+"F3.wireOp",EDGE,"E15");var subQ8=sQuery(id+"F3.wireOp",EDGE,"E5");var subQ9=sQuery(id+"F3.wireOp",EDGE,"E6");Q0=makeQuery(id+"F17.boolean.opBoolean","MERGE",FACE,{"derivedFrom":[makeQuery(id+"F8.boolean.opBoolean","SPLIT",FACE,{"disambiguationData":[TD([makeQuery(id+"F1.opExtrude","SWEPT_FACE",FACE,{"disambiguationData":[OSD([subQ5])]})])],"derivedFrom":makeQuery(id+"F4.boolean.opBoolean","MERGE",FACE,{"derivedFrom":[makeQuery(id+"F1.opExtrude","CAP_FACE",FACE,{"disambiguationData":[OSD([subQ5,subQ4,sQuery(id+"F0.wireOp",EDGE,"E2"),sQuery(id+"F0.wireOp",EDGE,"E3")])],"isStart":true}),makeQuery(id+"F4.opExtrude","CAP_FACE",FACE,{"disambiguationData":[OSD([subQ8,subQ9,subQ3,subQ2,subQ1,subQ0,sQuery(id+"F3.wireOp",EDGE,"E11"),sQuery(id+"F3.wireOp",EDGE,"E12"),subQ7,subQ6])],"isStart":true})]})}),makeQuery(id+"F17.opExtrude","CAP_FACE",FACE,{"disambiguationData":[OSD([sQuery(id+"F16.wireOp",EDGE,"E48"),sQuery(id+"F16.wireOp",EDGE,"E49.0"),sQuery(id+"F16.wireOp",EDGE,"E54"),sQuery(id+"F16.wireOp",EDGE,"E55")])],"isStart":true})]});}
            var sketch = newSketch(context, id + "F29", { "sketchPlane" : qUnion([Q0])});
            skLineSegment(sketch, "E74", {"start": v(-35, 11) * mm, "end": v(-35, 9) * mm, "construction": true});
            skLineSegment(sketch, "E75", {"start": v(-35, 10) * mm, "end": v(-23.1, 10) * mm, "construction": true});
            skLineSegment(sketch, "E76", {"start": v(-23.1, 15) * mm, "end": v(-23.1, 5) * mm, "construction": true});
            skCircle(sketch, "E77", {"center": v(-23.1, 15) * mm, "radius": 1.6 * mm});
            skCircle(sketch, "E78", {"center": v(-23.1, 5) * mm, "radius": 1.6 * mm});
            skSolve(sketch);
        }
        {
            var Q0;
            Q0 = qSketchRegion(id + "F29", true);
            extrude(context, id + "F30", {"entities" : qUnion([Q0]), "operationType" : NewBodyOperationType.REMOVE, "endBound" : BoundingType.THROUGH_ALL, "oppositeDirection" : true, "depth" : 25 * mm});
        }
        {
            var Q0;
            Q0=makeQuery(id+"F4.opExtrude","SWEPT_FACE",FACE,{"disambiguationData":[OSD([sQuery(id+"F3.wireOp",EDGE,"E7")])]});
            var sketch = newSketch(context, id + "F31", { "sketchPlane" : qUnion([Q0])});
            skLineSegment(sketch, "E79", {"start": v(11, 19.5) * mm, "end": v(10, 19.4) * mm});
            skLineSegment(sketch, "E80", {"start": v(10, 19.4) * mm, "end": v(10, 18.6) * mm});
            skLineSegment(sketch, "E81", {"start": v(10, 18.6) * mm, "end": v(11, 18.5) * mm});
            skLineSegment(sketch, "E82", {"start": v(11, 18.5) * mm, "end": v(11, 19.5) * mm});
            skLineSegment(sketch, "E83.0.1.0", {"start": v(11, 17.5) * mm, "end": v(10, 17.4) * mm});
            skLineSegment(sketch, "E83.0.1.1", {"start": v(11, 16.5) * mm, "end": v(11, 17.5) * mm});
            skLineSegment(sketch, "E83.0.1.2", {"start": v(10, 16.6) * mm, "end": v(11, 16.5) * mm});
            skLineSegment(sketch, "E83.0.1.3", {"start": v(10, 17.4) * mm, "end": v(10, 16.6) * mm});
            skLineSegment(sketch, "E83.0.2.0", {"start": v(11, 15.5) * mm, "end": v(10, 15.4) * mm});
            skLineSegment(sketch, "E83.0.2.1", {"start": v(11, 14.5) * mm, "end": v(11, 15.5) * mm});
            skLineSegment(sketch, "E83.0.2.2", {"start": v(10, 14.6) * mm, "end": v(11, 14.5) * mm});
            skLineSegment(sketch, "E83.0.2.3", {"start": v(10, 15.4) * mm, "end": v(10, 14.6) * mm});
            skLineSegment(sketch, "E83.0.3.0", {"start": v(11, 13.5) * mm, "end": v(10, 13.4) * mm});
            skLineSegment(sketch, "E83.0.3.1", {"start": v(11, 12.5) * mm, "end": v(11, 13.5) * mm});
            skLineSegment(sketch, "E83.0.3.2", {"start": v(10, 12.6) * mm, "end": v(11, 12.5) * mm});
            skLineSegment(sketch, "E83.0.3.3", {"start": v(10, 13.4) * mm, "end": v(10, 12.6) * mm});
            skLineSegment(sketch, "E83.0.4.0", {"start": v(11, 11.5) * mm, "end": v(10, 11.4) * mm});
            skLineSegment(sketch, "E83.0.4.1", {"start": v(11, 10.5) * mm, "end": v(11, 11.5) * mm});
            skLineSegment(sketch, "E83.0.4.2", {"start": v(10, 10.6) * mm, "end": v(11, 10.5) * mm});
            skLineSegment(sketch, "E83.0.4.3", {"start": v(10, 11.4) * mm, "end": v(10, 10.6) * mm});
            skLineSegment(sketch, "E83.0.5.0", {"start": v(11, 9.5) * mm, "end": v(10, 9.4) * mm});
            skLineSegment(sketch, "E83.0.5.1", {"start": v(11, 8.5) * mm, "end": v(11, 9.5) * mm});
            skLineSegment(sketch, "E83.0.5.2", {"start": v(10, 8.6) * mm, "end": v(11, 8.5) * mm});
            skLineSegment(sketch, "E83.0.5.3", {"start": v(10, 9.4) * mm, "end": v(10, 8.6) * mm});
            skLineSegment(sketch, "E83.0.6.0", {"start": v(11, 7.5) * mm, "end": v(10, 7.4) * mm});
            skLineSegment(sketch, "E83.0.6.1", {"start": v(11, 6.5) * mm, "end": v(11, 7.5) * mm});
            skLineSegment(sketch, "E83.0.6.2", {"start": v(10, 6.6) * mm, "end": v(11, 6.5) * mm});
            skLineSegment(sketch, "E83.0.6.3", {"start": v(10, 7.4) * mm, "end": v(10, 6.6) * mm});
            skLineSegment(sketch, "E83.0.7.0", {"start": v(11, 5.5) * mm, "end": v(10, 5.4) * mm});
            skLineSegment(sketch, "E83.0.7.1", {"start": v(11, 4.5) * mm, "end": v(11, 5.5) * mm});
            skLineSegment(sketch, "E83.0.7.2", {"start": v(10, 4.6) * mm, "end": v(11, 4.5) * mm});
            skLineSegment(sketch, "E83.0.7.3", {"start": v(10, 5.4) * mm, "end": v(10, 4.6) * mm});
            skLineSegment(sketch, "E83.0.8.0", {"start": v(11, 3.5) * mm, "end": v(10, 3.4) * mm});
            skLineSegment(sketch, "E83.0.8.1", {"start": v(11, 2.5) * mm, "end": v(11, 3.5) * mm});
            skLineSegment(sketch, "E83.0.8.2", {"start": v(10, 2.6) * mm, "end": v(11, 2.5) * mm});
            skLineSegment(sketch, "E83.0.8.3", {"start": v(10, 3.4) * mm, "end": v(10, 2.6) * mm});
            skLineSegment(sketch, "E83.0.9.0", {"start": v(11, 1.5) * mm, "end": v(10, 1.4) * mm});
            skLineSegment(sketch, "E83.0.9.1", {"start": v(11, 0.5) * mm, "end": v(11, 1.5) * mm});
            skLineSegment(sketch, "E83.0.9.2", {"start": v(10, 0.6) * mm, "end": v(11, 0.5) * mm});
            skLineSegment(sketch, "E83.0.9.3", {"start": v(10, 1.4) * mm, "end": v(10, 0.6) * mm});
            skLineSegment(sketch, "E83.direction1", {"start": v(11, 19.5) * mm, "end": v(36, 19.5) * mm, "construction": true});
            skLineSegment(sketch, "E83.direction2", {"start": v(11, 19.5) * mm, "end": v(11, 17.5) * mm, "construction": true});
            skSolve(sketch);
        }
        {
            var Q0;
            Q0 = qSketchRegion(id + "F31", true);
            extrude(context, id + "F32", {"entities" : qUnion([Q0]), "operationType" : NewBodyOperationType.ADD, "depth" : 8 * mm});
        }
        {
            var Q0;
            Q0=makeQuery(id+"F4.opExtrude","SWEPT_FACE",FACE,{"disambiguationData":[OSD([sQuery(id+"F3.wireOp",EDGE,"E15")])]});
            var sketch = newSketch(context, id + "F33", { "sketchPlane" : qUnion([Q0])});
            skLineSegment(sketch, "E84", {"start": v(35, 10) * mm, "end": v(31, 10) * mm, "construction": true});
            skCircle(sketch, "E85", {"center": v(31, 10) * mm, "radius": 1.7 * mm});
            skSolve(sketch);
        }
        {
            var Q0;
            Q0 = qSketchRegion(id + "F33", true);
            var Q1;
            Q1=makeQuery(id+"F4.opExtrude","SWEPT_FACE",FACE,{"disambiguationData":[OSD([sQuery(id+"F3.wireOp",EDGE,"E10")])]});
            extrude(context, id + "F34", {"entities" : qUnion([Q0]), "operationType" : NewBodyOperationType.REMOVE, "endBound" : BoundingType.UP_TO_SURFACE, "oppositeDirection" : true, "endBoundEntityFace" : qUnion([Q1]), "depth" : 25 * mm});
        }
        {
            var Q0;
            {var subQ0=sQuery(id+"F0.wireOp",EDGE,"E0");var subQ1=sQuery(id+"F0.wireOp",EDGE,"E1");var subQ2=sQuery(id+"F0.wireOp",EDGE,"E2");Q0=makeQuery(id+"F19.boolean.opBoolean","MERGE",FACE,{"derivedFrom":[makeQuery(id+"F8.boolean.opBoolean","SPLIT",FACE,{"disambiguationData":[TD([makeQuery(id+"F1.opExtrude","SWEPT_FACE",FACE,{"disambiguationData":[OSD([subQ0])]})])],"derivedFrom":makeQuery(id+"F1.opExtrude","CAP_FACE",FACE,{"disambiguationData":[OSD([subQ0,subQ1,subQ2,sQuery(id+"F0.wireOp",EDGE,"E3")])],"isStart":false})}),makeQuery(id+"F19.opExtrude","CAP_FACE",FACE,{"disambiguationData":[OSD([sQuery(id+"F18.wireOp",EDGE,"E58.0"),sQuery(id+"F18.wireOp",EDGE,"E59.0"),sQuery(id+"F18.wireOp",EDGE,"E60.0"),sQuery(id+"F18.wireOp",EDGE,"E61.0")])],"isStart":true})]});}
            var sketch = newSketch(context, id + "F35", { "sketchPlane" : qUnion([Q0])});
            skLineSegment(sketch, "E86.0", {"start": v(-35, -9) * mm, "end": v(-35, -1) * mm});
            skLineSegment(sketch, "E87.0", {"start": v(-19.3, -9) * mm, "end": v(-35, -9) * mm});
            skLineSegment(sketch, "E88.0", {"start": v(-19.3, -11) * mm, "end": v(-19.3, -9) * mm});
            skLineSegment(sketch, "E89.0", {"start": v(-35, -11) * mm, "end": v(-19.3, -11) * mm});
            skLineSegment(sketch, "E90.0", {"start": v(-35, -22) * mm, "end": v(-35, -11) * mm});
            skLineSegment(sketch, "E91.0", {"start": v(-12, -22) * mm, "end": v(-35, -22) * mm});
            skLineSegment(sketch, "E92", {"start": v(-12, -22) * mm, "end": v(-12, -1) * mm});
            skLineSegment(sketch, "E93", {"start": v(-12, -1) * mm, "end": v(-35, -1) * mm});
            skSolve(sketch);
        }
        {
            var Q0;
            Q0 = qSketchRegion(id + "F35", true);
            extrude(context, id + "F36", {"entities" : qUnion([Q0]), "oppositeDirection" : true, "depth" : 15 * mm});
        }
        {
            var Q0;
            Q0=makeQuery(id+"F36.opExtrude","CAP_FACE",FACE,{"disambiguationData":[OSD([sQuery(id+"F35.wireOp",EDGE,"E86.0"),sQuery(id+"F35.wireOp",EDGE,"E87.0"),sQuery(id+"F35.wireOp",EDGE,"E88.0"),sQuery(id+"F35.wireOp",EDGE,"E89.0"),sQuery(id+"F35.wireOp",EDGE,"E90.0"),sQuery(id+"F35.wireOp",EDGE,"E91.0"),sQuery(id+"F35.wireOp",EDGE,"E92"),sQuery(id+"F35.wireOp",EDGE,"E93")])],"isStart":true});
            var sketch = newSketch(context, id + "F37", { "sketchPlane" : qUnion([Q0])});
            skCircle(sketch, "E94.0", {"center": v(-23.1, -15) * mm, "radius": 1.6 * mm});
            skCircle(sketch, "E95.0", {"center": v(-23.1, -5) * mm, "radius": 1.6 * mm});
            skSolve(sketch);
        }
        {
            var Q0;
            Q0 = qSketchRegion(id + "F37", true);
            extrude(context, id + "F38", {"entities" : qUnion([Q0]), "operationType" : NewBodyOperationType.REMOVE, "endBound" : BoundingType.THROUGH_ALL, "oppositeDirection" : true, "depth" : 25 * mm});
        }
        {
            var Q0;
            Q0=makeQuery(id+"F36.opExtrude","SWEPT_FACE",FACE,{"disambiguationData":[OSD([sQuery(id+"F35.wireOp",EDGE,"E88.0")])]});
            var sketch = newSketch(context, id + "F39", { "sketchPlane" : qUnion([Q0])});
            skLineSegment(sketch, "E96", {"start": v(11, 27) * mm, "end": v(10, 26.9) * mm});
            skLineSegment(sketch, "E97", {"start": v(10, 26.9) * mm, "end": v(10, 26.1) * mm});
            skLineSegment(sketch, "E98", {"start": v(10, 26.1) * mm, "end": v(11, 26) * mm});
            skLineSegment(sketch, "E99", {"start": v(11, 26) * mm, "end": v(11, 27) * mm});
            skLineSegment(sketch, "E100", {"start": v(10, 26.5) * mm, "end": v(11, 26.5) * mm, "construction": true});
            skLineSegment(sketch, "E101.0.1.0", {"start": v(10, 28.1) * mm, "end": v(11, 28) * mm});
            skLineSegment(sketch, "E101.0.1.1", {"start": v(11, 28) * mm, "end": v(11, 29) * mm});
            skLineSegment(sketch, "E101.0.1.2", {"start": v(11, 29) * mm, "end": v(10, 28.9) * mm});
            skLineSegment(sketch, "E101.0.1.3", {"start": v(10, 28.9) * mm, "end": v(10, 28.1) * mm});
            skLineSegment(sketch, "E101.0.2.0", {"start": v(10, 30.1) * mm, "end": v(11, 30) * mm});
            skLineSegment(sketch, "E101.0.2.1", {"start": v(11, 30) * mm, "end": v(11, 31) * mm});
            skLineSegment(sketch, "E101.0.2.2", {"start": v(11, 31) * mm, "end": v(10, 30.9) * mm});
            skLineSegment(sketch, "E101.0.2.3", {"start": v(10, 30.9) * mm, "end": v(10, 30.1) * mm});
            skLineSegment(sketch, "E101.0.3.0", {"start": v(10, 32.1) * mm, "end": v(11, 32) * mm});
            skLineSegment(sketch, "E101.0.3.1", {"start": v(11, 32) * mm, "end": v(11, 33) * mm});
            skLineSegment(sketch, "E101.0.3.2", {"start": v(11, 33) * mm, "end": v(10, 32.9) * mm});
            skLineSegment(sketch, "E101.0.3.3", {"start": v(10, 32.9) * mm, "end": v(10, 32.1) * mm});
            skLineSegment(sketch, "E101.0.4.0", {"start": v(10, 34.1) * mm, "end": v(11, 34) * mm});
            skLineSegment(sketch, "E101.0.4.1", {"start": v(11, 34) * mm, "end": v(11, 35) * mm});
            skLineSegment(sketch, "E101.0.4.2", {"start": v(11, 35) * mm, "end": v(10, 34.9) * mm});
            skLineSegment(sketch, "E101.0.4.3", {"start": v(10, 34.9) * mm, "end": v(10, 34.1) * mm});
            skLineSegment(sketch, "E101.0.5.0", {"start": v(10, 36.1) * mm, "end": v(11, 36) * mm});
            skLineSegment(sketch, "E101.0.5.1", {"start": v(11, 36) * mm, "end": v(11, 37) * mm});
            skLineSegment(sketch, "E101.0.5.2", {"start": v(11, 37) * mm, "end": v(10, 36.9) * mm});
            skLineSegment(sketch, "E101.0.5.3", {"start": v(10, 36.9) * mm, "end": v(10, 36.1) * mm});
            skLineSegment(sketch, "E101.0.6.0", {"start": v(10, 38.1) * mm, "end": v(11, 38) * mm});
            skLineSegment(sketch, "E101.0.6.1", {"start": v(11, 38) * mm, "end": v(11, 39) * mm});
            skLineSegment(sketch, "E101.0.6.2", {"start": v(11, 39) * mm, "end": v(10, 38.9) * mm});
            skLineSegment(sketch, "E101.0.6.3", {"start": v(10, 38.9) * mm, "end": v(10, 38.1) * mm});
            skLineSegment(sketch, "E101.direction1", {"start": v(10, 26.1) * mm, "end": v(35, 26.1) * mm, "construction": true});
            skLineSegment(sketch, "E101.direction2", {"start": v(10, 26.1) * mm, "end": v(10, 28.1) * mm, "construction": true});
            skSolve(sketch);
        }
        {
            var Q0;
            Q0 = qSketchRegion(id + "F39", true);
            var Q1;
            Q1=makeQuery(id+"F32.opExtrude","CAP_FACE",FACE,{"disambiguationData":[OSD([sQuery(id+"F31.wireOp",EDGE,"E79"),sQuery(id+"F31.wireOp",EDGE,"E80"),sQuery(id+"F31.wireOp",EDGE,"E81"),sQuery(id+"F31.wireOp",EDGE,"E82")])],"isStart":false});
            extrude(context, id + "F40", {"entities" : qUnion([Q0]), "operationType" : NewBodyOperationType.ADD, "endBound" : BoundingType.UP_TO_SURFACE, "endBoundEntityFace" : qUnion([Q1]), "depth" : 25 * mm});
        }
        {
            var Q0;
            Q0=makeQuery(id+"F36.opExtrude","SWEPT_FACE",FACE,{"disambiguationData":[OSD([sQuery(id+"F35.wireOp",EDGE,"E91.0")])]});
            var sketch = newSketch(context, id + "F41", { "sketchPlane" : qUnion([Q0])});
            skCircle(sketch, "E102.0", {"center": v(-31, 10) * mm, "radius": 1.7 * mm, "construction": true});
            skLineSegment(sketch, "E103", {"start": v(-31, 10) * mm, "end": v(-31, 32.5) * mm, "construction": true});
            skPoint(sketch, "E103.endSnap0", {"position": v(-35, 32.5) * mm});
            skLineSegment(sketch, "E104", {"start": v(-31, 32.5) * mm, "end": v(-35, 32.5) * mm, "construction": true});
            skCircle(sketch, "E105", {"center": v(-31, 32.5) * mm, "radius": 1.7 * mm});
            skSolve(sketch);
        }
        {
            var Q0;
            Q0 = qSketchRegion(id + "F41", true);
            extrude(context, id + "F42", {"entities" : qUnion([Q0]), "operationType" : NewBodyOperationType.REMOVE, "endBound" : BoundingType.THROUGH_ALL, "oppositeDirection" : true, "depth" : 25 * mm});
        }
        {
            var Q0;
            Q0=makeQuery(id+"F23.boolean.opBoolean","COPY",EDGE,{"derivedFrom":makeQuery(id+"F23.opExtrude","CAP_EDGE",EDGE,{"disambiguationData":[OSD([sQuery(id+"F22.wireOp",EDGE,"E64.0.1")])],"isStart":true})});
            var Q1;
            Q1=makeQuery(id+"F23.boolean.opBoolean","COPY",EDGE,{"derivedFrom":makeQuery(id+"F23.opExtrude","CAP_EDGE",EDGE,{"disambiguationData":[OSD([sQuery(id+"F22.wireOp",EDGE,"E64.0.0")])],"isStart":true})});
            var Q2;
            Q2=makeQuery(id+"F23.boolean.opBoolean","COPY",EDGE,{"derivedFrom":makeQuery(id+"F23.opExtrude","CAP_EDGE",EDGE,{"disambiguationData":[OSD([sQuery(id+"F22.wireOp",EDGE,"E64.0.3")])],"isStart":true})});
            var Q3;
            Q3=makeQuery(id+"F23.boolean.opBoolean","COPY",EDGE,{"derivedFrom":makeQuery(id+"F23.opExtrude","CAP_EDGE",EDGE,{"disambiguationData":[OSD([sQuery(id+"F22.wireOp",EDGE,"E64.0.2")])],"isStart":true})});
            var Q4;
            Q4=makeQuery(id+"F8.boolean.opBoolean","COPY",EDGE,{"derivedFrom":makeQuery(id+"F8.opExtrude","CAP_EDGE",EDGE,{"disambiguationData":[OSD([sQuery(id+"F7.wireOp",EDGE,"E27")])],"isStart":true})});
            var Q5;
            Q5=makeQuery(id+"F8.boolean.opBoolean","COPY",EDGE,{"disambiguationData":[OD(0.0)],"derivedFrom":makeQuery(id+"F8.opExtrude","SWEPT_EDGE",EDGE,{"disambiguationData":[OSD([sQuery(id+"F0.wireOp",EDGE,"E1"),sQuery(id+"F7.wireOp",EDGE,"E25"),sQuery(id+"F7.wireOp",EDGE,"E27")])]})});
            var Q6;
            {var subQ0=sQuery(id+"F5.wireOp",EDGE,"E21");Q6=makeQuery(id+"F8.boolean.opBoolean","SPLIT",EDGE,{"disambiguationData":[TD([makeQuery(id+"F8.opExtrude","SWEPT_FACE",FACE,{"disambiguationData":[OSD([sQuery(id+"F7.wireOp",EDGE,"E27")])]})])],"derivedFrom":makeQuery(id+"F6.boolean.opBoolean","COPY",EDGE,{"derivedFrom":makeQuery(id+"F6.opExtrude","CAP_EDGE",EDGE,{"disambiguationData":[OSD([subQ0])],"isStart":true})})});}
            var Q7;
            Q7=makeQuery(id+"F8.boolean.opBoolean","INTERSECT",EDGE,{"disambiguationData":[OD(1.0)],"derivedFrom":[makeQuery(id+"F6.boolean.opBoolean","COPY",FACE,{"derivedFrom":makeQuery(id+"F6.opExtrude","SWEPT_FACE",FACE,{"disambiguationData":[OSD([sQuery(id+"F5.wireOp",EDGE,"E21")])]})}),makeQuery(id+"F8.opExtrude","SWEPT_FACE",FACE,{"disambiguationData":[OSD([sQuery(id+"F7.wireOp",EDGE,"E27")])]})]});
            var Q8;
            Q8=makeQuery(id+"F8.boolean.opBoolean","INTERSECT",EDGE,{"disambiguationData":[OD(0.0)],"derivedFrom":[makeQuery(id+"F6.boolean.opBoolean","COPY",FACE,{"derivedFrom":makeQuery(id+"F6.opExtrude","SWEPT_FACE",FACE,{"disambiguationData":[OSD([sQuery(id+"F5.wireOp",EDGE,"E21")])]})}),makeQuery(id+"F8.opExtrude","SWEPT_FACE",FACE,{"disambiguationData":[OSD([sQuery(id+"F7.wireOp",EDGE,"E27")])]})]});
            var Q9;
            Q9=makeQuery(id+"F4.opExtrude","CAP_EDGE",EDGE,{"disambiguationData":[OSD([sQuery(id+"F3.wireOp",EDGE,"E10")])],"isStart":true});
            var Q10;
            Q10=makeQuery(id+"F8.boolean.opBoolean","COPY",EDGE,{"derivedFrom":makeQuery(id+"F8.opExtrude","SWEPT_EDGE",EDGE,{"disambiguationData":[OSD([sQuery(id+"F3.wireOp",EDGE,"E10"),sQuery(id+"F7.wireOp",EDGE,"E30"),sQuery(id+"F7.wireOp",EDGE,"E31")])]})});
            var Q11;
            Q11=makeQuery(id+"F4.opExtrude","TWEAK_EDGE",EDGE,{"derivedFrom":[dummyQuery(id+"F2.planeOp",FACE),makeQuery(id+"F3.imprint","IMPRINT",EDGE,{"derivedFrom":sQuery(id+"F3.wireOp",EDGE,"E10")})]});
            var Q12;
            Q12=makeQuery(id+"F4.opExtrude","SWEPT_EDGE",EDGE,{"disambiguationData":[OSD([sQuery(id+"F3.wireOp",EDGE,"E9"),sQuery(id+"F3.wireOp",EDGE,"E10")])]});
            var Q13;
            Q13=makeQuery(id+"F4.opExtrude","CAP_EDGE",EDGE,{"disambiguationData":[OSD([sQuery(id+"F3.wireOp",EDGE,"E9")])],"isStart":true});
            var Q14;
            Q14=makeQuery(id+"F4.opExtrude","TWEAK_EDGE",EDGE,{"derivedFrom":[dummyQuery(id+"F2.planeOp",FACE),makeQuery(id+"F3.imprint","IMPRINT",EDGE,{"derivedFrom":sQuery(id+"F3.wireOp",EDGE,"E9")})]});
            var Q15;
            Q15=makeQuery(id+"F4.opExtrude","SWEPT_EDGE",EDGE,{"disambiguationData":[OSD([sQuery(id+"F3.wireOp",EDGE,"E8"),sQuery(id+"F3.wireOp",EDGE,"E9")])]});
            var Q16;
            Q16=makeQuery(id+"F4.opExtrude","SWEPT_EDGE",EDGE,{"disambiguationData":[OSD([sQuery(id+"F3.wireOp",EDGE,"E5"),sQuery(id+"F3.wireOp",EDGE,"E6")])]});
            var Q17;
            Q17=makeQuery(id+"F4.opExtrude","TWEAK_EDGE",EDGE,{"derivedFrom":[dummyQuery(id+"F2.planeOp",FACE),makeQuery(id+"F3.imprint","IMPRINT",EDGE,{"derivedFrom":sQuery(id+"F3.wireOp",EDGE,"E5")})]});
            var Q18;
            Q18=makeQuery(id+"F4.opExtrude","CAP_EDGE",EDGE,{"disambiguationData":[OSD([sQuery(id+"F3.wireOp",EDGE,"E5")])],"isStart":true});
            var Q19;
            Q19=makeQuery(id+"F4.opExtrude","SWEPT_EDGE",EDGE,{"disambiguationData":[OSD([sQuery(id+"F3.wireOp",EDGE,"E5"),sQuery(id+"F3.wireOp",EDGE,"E15")])]});
            var Q20;
            Q20=makeQuery(id+"F4.opExtrude","CAP_EDGE",EDGE,{"disambiguationData":[OSD([sQuery(id+"F3.wireOp",EDGE,"E6")])],"isStart":true});
            var Q21;
            Q21=makeQuery(id+"F4.opExtrude","CAP_EDGE",EDGE,{"disambiguationData":[OSD([sQuery(id+"F3.wireOp",EDGE,"E15")])],"isStart":true});
            var Q22;
            Q22=makeQuery(id+"F17.opExtrude","CAP_EDGE",EDGE,{"disambiguationData":[OSD([sQuery(id+"F16.wireOp",EDGE,"E48")])],"isStart":true});
            var Q23;
            {var subQ0=sQuery(id+"F3.wireOp",EDGE,"E10");var subQ1=sQuery(id+"F3.wireOp",EDGE,"E9");var subQ2=sQuery(id+"F3.wireOp",EDGE,"E8");var subQ3=sQuery(id+"F3.wireOp",EDGE,"E7");var subQ4=sQuery(id+"F0.wireOp",EDGE,"E1");var subQ5=sQuery(id+"F0.wireOp",EDGE,"E0");var subQ6=sQuery(id+"F3.wireOp",EDGE,"E16");var subQ7=sQuery(id+"F3.wireOp",EDGE,"E15");var subQ8=sQuery(id+"F3.wireOp",EDGE,"E5");var subQ9=sQuery(id+"F3.wireOp",EDGE,"E6");Q23=makeQuery(id+"F13.opFillet","BLEND_EDGE",EDGE,{"blendedFrom":[makeQuery(id+"F1.opExtrude","SWEPT_EDGE",EDGE,{"disambiguationData":[OSD([subQ5,subQ4])]}),makeQuery(id+"F8.boolean.opBoolean","SPLIT",FACE,{"disambiguationData":[TD([makeQuery(id+"F1.opExtrude","SWEPT_FACE",FACE,{"disambiguationData":[OSD([subQ5])]})])],"derivedFrom":makeQuery(id+"F4.boolean.opBoolean","MERGE",FACE,{"derivedFrom":[makeQuery(id+"F1.opExtrude","CAP_FACE",FACE,{"disambiguationData":[OSD([subQ5,subQ4,sQuery(id+"F0.wireOp",EDGE,"E2"),sQuery(id+"F0.wireOp",EDGE,"E3")])],"isStart":true}),makeQuery(id+"F4.opExtrude","CAP_FACE",FACE,{"disambiguationData":[OSD([subQ8,subQ9,subQ3,subQ2,subQ1,subQ0,sQuery(id+"F3.wireOp",EDGE,"E11"),sQuery(id+"F3.wireOp",EDGE,"E12"),subQ7,subQ6])],"isStart":true})]})})],"blendedInto":[makeQuery(id+"F8.boolean.opBoolean","SPLIT",FACE,{"disambiguationData":[TD([makeQuery(id+"F1.opExtrude","SWEPT_FACE",FACE,{"disambiguationData":[OSD([subQ5])]})])],"derivedFrom":makeQuery(id+"F4.boolean.opBoolean","MERGE",FACE,{"derivedFrom":[makeQuery(id+"F1.opExtrude","CAP_FACE",FACE,{"disambiguationData":[OSD([subQ5,subQ4,sQuery(id+"F0.wireOp",EDGE,"E2"),sQuery(id+"F0.wireOp",EDGE,"E3")])],"isStart":true}),makeQuery(id+"F4.opExtrude","CAP_FACE",FACE,{"disambiguationData":[OSD([subQ8,subQ9,subQ3,subQ2,subQ1,subQ0,sQuery(id+"F3.wireOp",EDGE,"E11"),sQuery(id+"F3.wireOp",EDGE,"E12"),subQ7,subQ6])],"isStart":true})]})})]});}
            var Q24;
            {var subQ0=sQuery(id+"F0.wireOp",EDGE,"E0");var subQ1=sQuery(id+"F0.wireOp",EDGE,"E1");var subQ2=sQuery(id+"F0.wireOp",EDGE,"E2");Q24=makeQuery(id+"F13.opFillet","BLEND_EDGE",EDGE,{"blendedFrom":[makeQuery(id+"F1.opExtrude","SWEPT_EDGE",EDGE,{"disambiguationData":[OSD([subQ0,subQ1])]}),makeQuery(id+"F8.boolean.opBoolean","SPLIT",FACE,{"disambiguationData":[TD([makeQuery(id+"F1.opExtrude","SWEPT_FACE",FACE,{"disambiguationData":[OSD([subQ0])]})])],"derivedFrom":makeQuery(id+"F1.opExtrude","CAP_FACE",FACE,{"disambiguationData":[OSD([subQ0,subQ1,subQ2,sQuery(id+"F0.wireOp",EDGE,"E3")])],"isStart":false})})],"blendedInto":[makeQuery(id+"F8.boolean.opBoolean","SPLIT",FACE,{"disambiguationData":[TD([makeQuery(id+"F1.opExtrude","SWEPT_FACE",FACE,{"disambiguationData":[OSD([subQ0])]})])],"derivedFrom":makeQuery(id+"F1.opExtrude","CAP_FACE",FACE,{"disambiguationData":[OSD([subQ0,subQ1,subQ2,sQuery(id+"F0.wireOp",EDGE,"E3")])],"isStart":false})})]});}
            var Q25;
            Q25=makeQuery(id+"F8.boolean.opBoolean","COPY",EDGE,{"disambiguationData":[OD(1.0)],"derivedFrom":makeQuery(id+"F8.opExtrude","SWEPT_EDGE",EDGE,{"disambiguationData":[OSD([sQuery(id+"F0.wireOp",EDGE,"E1"),sQuery(id+"F7.wireOp",EDGE,"E25"),sQuery(id+"F7.wireOp",EDGE,"E27")])]})});
            var Q26;
            Q26=makeQuery(id+"F8.boolean.opBoolean","COPY",EDGE,{"disambiguationData":[OD(1.0)],"derivedFrom":makeQuery(id+"F8.opExtrude","SWEPT_EDGE",EDGE,{"disambiguationData":[OSD([sQuery(id+"F7.wireOp",EDGE,"E27"),sQuery(id+"F7.wireOp",EDGE,"E32.filletArc")])]})});
            var Q27;
            Q27=makeQuery(id+"F8.boolean.opBoolean","INTERSECT",EDGE,{"derivedFrom":[makeQuery(id+"F1.opExtrude","CAP_FACE",FACE,{"disambiguationData":[OSD([sQuery(id+"F0.wireOp",EDGE,"E0"),sQuery(id+"F0.wireOp",EDGE,"E1"),sQuery(id+"F0.wireOp",EDGE,"E2"),sQuery(id+"F0.wireOp",EDGE,"E3")])],"isStart":false}),makeQuery(id+"F8.opExtrude","SWEPT_FACE",FACE,{"disambiguationData":[OSD([sQuery(id+"F7.wireOp",EDGE,"E27")])]})]});
            var Q28;
            Q28=makeQuery(id+"F8.boolean.opBoolean","INTERSECT",EDGE,{"derivedFrom":[makeQuery(id+"F4.opExtrude","CAP_FACE",FACE,{"disambiguationData":[OSD([dummyQuery(id+"F2.planeOp",FACE)])],"isStart":false}),makeQuery(id+"F8.opExtrude","SWEPT_FACE",FACE,{"disambiguationData":[OSD([sQuery(id+"F7.wireOp",EDGE,"E31")])]})]});
            var Q29;
            Q29=makeQuery(id+"F6.boolean.opBoolean","INTERSECT",EDGE,{"disambiguationData":[OD(0.0)],"derivedFrom":[makeQuery(id+"F4.opExtrude","CAP_FACE",FACE,{"disambiguationData":[OSD([dummyQuery(id+"F2.planeOp",FACE)])],"isStart":false}),makeQuery(id+"F6.opExtrude","SWEPT_FACE",FACE,{"disambiguationData":[OSD([sQuery(id+"F5.wireOp",EDGE,"E21")])]})]});
            var Q30;
            Q30=makeQuery(id+"F8.boolean.opBoolean","SPLIT",EDGE,{"derivedFrom":makeQuery(id+"F6.boolean.opBoolean","INTERSECT",EDGE,{"derivedFrom":[makeQuery(id+"F1.opExtrude","SWEPT_FACE",FACE,{"disambiguationData":[OSD([sQuery(id+"F0.wireOp",EDGE,"E2")])]}),makeQuery(id+"F6.opExtrude","SWEPT_FACE",FACE,{"disambiguationData":[OSD([sQuery(id+"F5.wireOp",EDGE,"E21")])]})]})});
            var Q31;
            {var subQ0=dummyQuery(id+"F2.planeOp",FACE);Q31=makeQuery(id+"F6.boolean.opBoolean","SPLIT",EDGE,{"disambiguationData":[TD([makeQuery(id+"F1.opExtrude","SWEPT_FACE",FACE,{"disambiguationData":[OSD([sQuery(id+"F0.wireOp",EDGE,"E0")])]})])],"derivedFrom":makeQuery(id+"F4.opExtrude","TWEAK_EDGE",EDGE,{"derivedFrom":[subQ0,makeQuery(id+"F3.imprint","IMPRINT",EDGE,{"derivedFrom":sQuery(id+"F3.wireOp",EDGE,"E11")})]})});}
            var Q32;
            Q32=makeQuery(id+"F4.opExtrude","TWEAK_EDGE",EDGE,{"derivedFrom":[dummyQuery(id+"F2.planeOp",FACE),makeQuery(id+"F3.imprint","IMPRINT",EDGE,{"derivedFrom":sQuery(id+"F3.wireOp",EDGE,"E12")})]});
            var Q33;
            Q33=makeQuery(id+"F1.opExtrude","SWEPT_EDGE",EDGE,{"disambiguationData":[OSD([sQuery(id+"F0.wireOp",EDGE,"E0"),sQuery(id+"F0.wireOp",EDGE,"E2")])]});
            var Q34;
            {var subQ0=sQuery(id+"F0.wireOp",EDGE,"E2");var subQ1=sQuery(id+"F0.wireOp",EDGE,"E0");Q34=makeQuery(id+"F8.boolean.opBoolean","SPLIT",EDGE,{"disambiguationData":[TD([makeQuery(id+"F1.opExtrude","SWEPT_FACE",FACE,{"disambiguationData":[OSD([subQ1])]})])],"derivedFrom":makeQuery(id+"F1.opExtrude","CAP_EDGE",EDGE,{"disambiguationData":[OSD([subQ0])],"isStart":false})});}
            var Q35;
            {var subQ0=sQuery(id+"F0.wireOp",EDGE,"E0");var subQ1=sQuery(id+"F0.wireOp",EDGE,"E2");Q35=makeQuery(id+"F12.boolean.opBoolean","SPLIT",EDGE,{"disambiguationData":[TD([makeQuery(id+"F8.boolean.opBoolean","COPY",FACE,{"derivedFrom":makeQuery(id+"F1.opExtrude","SWEPT_FACE",FACE,{"disambiguationData":[OSD([subQ1])]})})])],"derivedFrom":makeQuery(id+"F1.opExtrude","CAP_EDGE",EDGE,{"disambiguationData":[OSD([subQ0])],"isStart":false})});}
            var Q36;
            Q36=makeQuery(id+"F4.opExtrude","TWEAK_EDGE",EDGE,{"derivedFrom":[dummyQuery(id+"F2.planeOp",FACE),makeQuery(id+"F3.imprint","IMPRINT",EDGE,{"derivedFrom":sQuery(id+"F3.wireOp",EDGE,"E15")})]});
            var Q37;
            Q37=makeQuery(id+"F4.opExtrude","TWEAK_EDGE",EDGE,{"derivedFrom":[dummyQuery(id+"F2.planeOp",FACE),makeQuery(id+"F3.imprint","IMPRINT",EDGE,{"derivedFrom":sQuery(id+"F3.wireOp",EDGE,"E8")})]});
            var Q38;
            Q38=makeQuery(id+"F4.opExtrude","TWEAK_EDGE",EDGE,{"derivedFrom":[dummyQuery(id+"F2.planeOp",FACE),makeQuery(id+"F3.imprint","IMPRINT",EDGE,{"derivedFrom":sQuery(id+"F3.wireOp",EDGE,"E6")})]});
            var Q39;
            Q39=makeQuery(id+"F4.opExtrude","CAP_EDGE",EDGE,{"disambiguationData":[OSD([sQuery(id+"F3.wireOp",EDGE,"E8")])],"isStart":true});
            var Q40;
            Q40=makeQuery(id+"F4.opExtrude","CAP_EDGE",EDGE,{"disambiguationData":[OSD([sQuery(id+"F3.wireOp",EDGE,"E7")])],"isStart":true});
            var Q41;
            Q41=makeQuery(id+"F4.opExtrude","TWEAK_EDGE",EDGE,{"derivedFrom":[dummyQuery(id+"F2.planeOp",FACE),makeQuery(id+"F3.imprint","IMPRINT",EDGE,{"derivedFrom":sQuery(id+"F3.wireOp",EDGE,"E7")})]});
            var Q42;
            Q42=makeQuery(id+"F19.opExtrude","CAP_EDGE",EDGE,{"disambiguationData":[OSD([sQuery(id+"F18.wireOp",EDGE,"E58.0")])],"isStart":true});
            var Q43;
            Q43=makeQuery(id+"F19.opExtrude","SWEPT_EDGE",EDGE,{"disambiguationData":[OSD([sQuery(id+"F18.wireOp",EDGE,"E58.0"),sQuery(id+"F18.wireOp",EDGE,"E60.0")])]});
            var Q44;
            Q44=makeQuery(id+"F19.opExtrude","CAP_EDGE",EDGE,{"disambiguationData":[OSD([sQuery(id+"F18.wireOp",EDGE,"E60.0")])],"isStart":true});
            var Q45;
            Q45=makeQuery(id+"F19.opExtrude","CAP_EDGE",EDGE,{"disambiguationData":[OSD([sQuery(id+"F18.wireOp",EDGE,"E59.0")])],"isStart":true});
            var Q46;
            Q46=makeQuery(id+"F19.opExtrude","SWEPT_EDGE",EDGE,{"disambiguationData":[OSD([sQuery(id+"F18.wireOp",EDGE,"E58.0"),sQuery(id+"F18.wireOp",EDGE,"E59.0")])]});
            var Q47;
            Q47=makeQuery(id+"F17.opExtrude","SWEPT_EDGE",EDGE,{"disambiguationData":[OSD([sQuery(id+"F16.wireOp",EDGE,"E48"),sQuery(id+"F16.wireOp",EDGE,"E54")])]});
            var Q48;
            Q48=makeQuery(id+"F17.opExtrude","CAP_EDGE",EDGE,{"disambiguationData":[OSD([sQuery(id+"F16.wireOp",EDGE,"E54")])],"isStart":true});
            var Q49;
            Q49=makeQuery(id+"F17.opExtrude","CAP_EDGE",EDGE,{"disambiguationData":[OSD([sQuery(id+"F16.wireOp",EDGE,"E55")])],"isStart":true});
            var Q50;
            Q50=makeQuery(id+"F17.opExtrude","SWEPT_EDGE",EDGE,{"disambiguationData":[OSD([sQuery(id+"F16.wireOp",EDGE,"E48"),sQuery(id+"F16.wireOp",EDGE,"E55")])]});
            var Q51;
            {var subQ0=sQuery(id+"F9.wireOp",EDGE,"E33");var subQ1=sQuery(id+"F11.wireOp",EDGE,"E36");Q51=makeQuery(id+"F17.boolean.opBoolean","MERGE",EDGE,{"derivedFrom":[makeQuery(id+"F15.boolean.opBoolean","SPLIT",EDGE,{"disambiguationData":[TD([makeQuery(id+"F15.opExtrude","SWEPT_FACE",FACE,{"disambiguationData":[OSD([sQuery(id+"F14.wireOp",EDGE,"E42.rect.top")])]})])],"derivedFrom":makeQuery(id+"F12.boolean.opBoolean","COPY",EDGE,{"derivedFrom":makeQuery(id+"F12.opExtrude","SWEPT_EDGE",EDGE,{"disambiguationData":[OSD([subQ0,subQ1,sQuery(id+"F11.wireOp",EDGE,"E41")])]})})}),makeQuery(id+"F17.opExtrude","SWEPT_EDGE",EDGE,{"disambiguationData":[OSD([sQuery(id+"F16.wireOp",EDGE,"E49.0"),sQuery(id+"F16.wireOp",EDGE,"E53"),sQuery(id+"F16.wireOp",EDGE,"E55")])]})]});}
            var Q52;
            {var subQ0=sQuery(id+"F9.wireOp",EDGE,"E33");var subQ1=sQuery(id+"F11.wireOp",EDGE,"E38");Q52=makeQuery(id+"F17.boolean.opBoolean","MERGE",EDGE,{"derivedFrom":[makeQuery(id+"F15.boolean.opBoolean","SPLIT",EDGE,{"disambiguationData":[TD([makeQuery(id+"F15.opExtrude","SWEPT_FACE",FACE,{"disambiguationData":[OSD([sQuery(id+"F14.wireOp",EDGE,"E42.rect.top")])]})])],"derivedFrom":makeQuery(id+"F12.boolean.opBoolean","COPY",EDGE,{"derivedFrom":makeQuery(id+"F12.opExtrude","SWEPT_EDGE",EDGE,{"disambiguationData":[OSD([subQ0,subQ1,sQuery(id+"F11.wireOp",EDGE,"E41")])]})})}),makeQuery(id+"F17.opExtrude","SWEPT_EDGE",EDGE,{"disambiguationData":[OSD([sQuery(id+"F16.wireOp",EDGE,"E49.0"),sQuery(id+"F16.wireOp",EDGE,"E52"),sQuery(id+"F16.wireOp",EDGE,"E54")])]})]});}
            var Q53;
            {var subQ0=sQuery(id+"F9.wireOp",EDGE,"E33");var subQ1=sQuery(id+"F11.wireOp",EDGE,"E36");var subQ2=sQuery(id+"F0.wireOp",EDGE,"E0");var subQ3=sQuery(id+"F0.wireOp",EDGE,"E1");var subQ4=sQuery(id+"F0.wireOp",EDGE,"E2");var subQ5=sQuery(id+"F0.wireOp",EDGE,"E3");Q53=makeQuery(id+"F19.boolean.opBoolean","MERGE",EDGE,{"derivedFrom":[makeQuery(id+"F15.boolean.opBoolean","SPLIT",EDGE,{"disambiguationData":[TD([makeQuery(id+"F15.opExtrude","SWEPT_FACE",FACE,{"disambiguationData":[OSD([sQuery(id+"F14.wireOp",EDGE,"E42.rect.bottom")])]})])],"derivedFrom":makeQuery(id+"F12.boolean.opBoolean","COPY",EDGE,{"derivedFrom":makeQuery(id+"F12.opExtrude","SWEPT_EDGE",EDGE,{"disambiguationData":[OSD([subQ0,subQ1,sQuery(id+"F11.wireOp",EDGE,"E41")])]})})}),makeQuery(id+"F19.opExtrude","SWEPT_EDGE",EDGE,{"disambiguationData":[OSD([subQ2,subQ3,subQ4,subQ5,subQ1,sQuery(id+"F18.wireOp",EDGE,"E60.0"),sQuery(id+"F18.wireOp",EDGE,"E61.0")])]})]});}
            var Q54;
            Q54=makeQuery(id+"F21.boolean.opBoolean","COPY",EDGE,{"derivedFrom":makeQuery(id+"F21.opExtrude","CAP_EDGE",EDGE,{"disambiguationData":[OSD([sQuery(id+"F20.wireOp",EDGE,"E63.rect.top")])],"isStart":true})});
            var Q55;
            Q55=makeQuery(id+"F21.boolean.opBoolean","COPY",EDGE,{"derivedFrom":makeQuery(id+"F21.opExtrude","CAP_EDGE",EDGE,{"disambiguationData":[OSD([sQuery(id+"F20.wireOp",EDGE,"E63.rect.right")])],"isStart":true})});
            var Q56;
            Q56=makeQuery(id+"F21.boolean.opBoolean","COPY",EDGE,{"derivedFrom":makeQuery(id+"F21.opExtrude","CAP_EDGE",EDGE,{"disambiguationData":[OSD([sQuery(id+"F20.wireOp",EDGE,"E63.rect.left")])],"isStart":true})});
            var Q57;
            Q57=makeQuery(id+"F21.boolean.opBoolean","COPY",EDGE,{"derivedFrom":makeQuery(id+"F21.opExtrude","CAP_EDGE",EDGE,{"disambiguationData":[OSD([sQuery(id+"F20.wireOp",EDGE,"E63.rect.bottom")])],"isStart":true})});
            var Q58;
            Q58=makeQuery(id+"F25.boolean.opBoolean","INTERSECT",EDGE,{"derivedFrom":[makeQuery(id+"F8.boolean.opBoolean","COPY",FACE,{"disambiguationData":[OD(1.0)],"derivedFrom":makeQuery(id+"F8.opExtrude","SWEPT_FACE",FACE,{"disambiguationData":[OSD([sQuery(id+"F7.wireOp",EDGE,"E27")])]})}),makeQuery(id+"F25.opExtrude","SWEPT_FACE",FACE,{"disambiguationData":[OSD([sQuery(id+"F24.wireOp",EDGE,"E71")])]})]});
            var Q59;
            Q59=makeQuery(id+"F25.boolean.opBoolean","INTERSECT",EDGE,{"derivedFrom":[makeQuery(id+"F8.boolean.opBoolean","COPY",FACE,{"disambiguationData":[OD(0.0)],"derivedFrom":makeQuery(id+"F8.opExtrude","SWEPT_FACE",FACE,{"disambiguationData":[OSD([sQuery(id+"F7.wireOp",EDGE,"E27")])]})}),makeQuery(id+"F25.opExtrude","SWEPT_FACE",FACE,{"disambiguationData":[OSD([sQuery(id+"F24.wireOp",EDGE,"E70")])]})]});
            var Q60;
            Q60=makeQuery(id+"F25.boolean.opBoolean","INTERSECT",EDGE,{"derivedFrom":[makeQuery(id+"F23.boolean.opBoolean","COPY",FACE,{"derivedFrom":makeQuery(id+"F23.opExtrude","SWEPT_FACE",FACE,{"disambiguationData":[OSD([sQuery(id+"F22.wireOp",EDGE,"E64.0.1")])]})}),makeQuery(id+"F25.opExtrude","SWEPT_FACE",FACE,{"disambiguationData":[OSD([sQuery(id+"F24.wireOp",EDGE,"E70")])]})]});
            var Q61;
            Q61=makeQuery(id+"F25.boolean.opBoolean","INTERSECT",EDGE,{"derivedFrom":[makeQuery(id+"F23.boolean.opBoolean","COPY",FACE,{"derivedFrom":makeQuery(id+"F23.opExtrude","SWEPT_FACE",FACE,{"disambiguationData":[OSD([sQuery(id+"F22.wireOp",EDGE,"E64.0.3")])]})}),makeQuery(id+"F25.opExtrude","SWEPT_FACE",FACE,{"disambiguationData":[OSD([sQuery(id+"F24.wireOp",EDGE,"E70")])]})]});
            var Q62;
            Q62=makeQuery(id+"F25.boolean.opBoolean","INTERSECT",EDGE,{"derivedFrom":[makeQuery(id+"F21.boolean.opBoolean","COPY",FACE,{"derivedFrom":makeQuery(id+"F21.opExtrude","SWEPT_FACE",FACE,{"disambiguationData":[OSD([sQuery(id+"F20.wireOp",EDGE,"E63.rect.top")])]})}),makeQuery(id+"F25.opExtrude","SWEPT_FACE",FACE,{"disambiguationData":[OSD([sQuery(id+"F24.wireOp",EDGE,"E71")])]})]});
            var Q63;
            Q63=makeQuery(id+"F25.boolean.opBoolean","INTERSECT",EDGE,{"derivedFrom":[makeQuery(id+"F21.boolean.opBoolean","COPY",FACE,{"derivedFrom":makeQuery(id+"F21.opExtrude","SWEPT_FACE",FACE,{"disambiguationData":[OSD([sQuery(id+"F20.wireOp",EDGE,"E63.rect.bottom")])]})}),makeQuery(id+"F25.opExtrude","SWEPT_FACE",FACE,{"disambiguationData":[OSD([sQuery(id+"F24.wireOp",EDGE,"E71")])]})]});
            var Q64;
            Q64=makeQuery(id+"F30.boolean.opBoolean","COPY",EDGE,{"derivedFrom":makeQuery(id+"F30.opExtrude","CAP_EDGE",EDGE,{"disambiguationData":[OSD([sQuery(id+"F29.wireOp",EDGE,"E77")])],"isStart":true})});
            var Q65;
            Q65=makeQuery(id+"F30.boolean.opBoolean","COPY",EDGE,{"derivedFrom":makeQuery(id+"F30.opExtrude","CAP_EDGE",EDGE,{"disambiguationData":[OSD([sQuery(id+"F29.wireOp",EDGE,"E78")])],"isStart":true})});
            var Q66;
            Q66=makeQuery(id+"F30.boolean.opBoolean","INTERSECT",EDGE,{"derivedFrom":[makeQuery(id+"F4.opExtrude","CAP_FACE",FACE,{"disambiguationData":[OSD([dummyQuery(id+"F2.planeOp",FACE)])],"isStart":false}),makeQuery(id+"F30.opExtrude","SWEPT_FACE",FACE,{"disambiguationData":[OSD([sQuery(id+"F29.wireOp",EDGE,"E77")])]})]});
            var Q67;
            Q67=makeQuery(id+"F30.boolean.opBoolean","INTERSECT",EDGE,{"derivedFrom":[makeQuery(id+"F4.opExtrude","CAP_FACE",FACE,{"disambiguationData":[OSD([dummyQuery(id+"F2.planeOp",FACE)])],"isStart":false}),makeQuery(id+"F30.opExtrude","SWEPT_FACE",FACE,{"disambiguationData":[OSD([sQuery(id+"F29.wireOp",EDGE,"E78")])]})]});
            var Q68;
            Q68=makeQuery(id+"F34.boolean.opBoolean","COPY",EDGE,{"derivedFrom":makeQuery(id+"F34.opExtrude","CAP_EDGE",EDGE,{"disambiguationData":[OSD([sQuery(id+"F33.wireOp",EDGE,"E85")])],"isStart":true})});
            var Q69;
            Q69=makeQuery(id+"F34.boolean.opBoolean","COPY",EDGE,{"derivedFrom":makeQuery(id+"F34.opExtrude","TWEAK_EDGE",EDGE,{"derivedFrom":[makeQuery(id+"F4.opExtrude","SWEPT_FACE",FACE,{"disambiguationData":[OSD([sQuery(id+"F3.wireOp",EDGE,"E10")])]}),makeQuery(id+"F33.imprint","IMPRINT",EDGE,{"derivedFrom":sQuery(id+"F33.wireOp",EDGE,"E85")})]})});
            var Q70;
            Q70=makeQuery(id+"F36.opExtrude","CAP_EDGE",EDGE,{"disambiguationData":[OSD([sQuery(id+"F35.wireOp",EDGE,"E89.0")])],"isStart":true});
            var Q71;
            Q71=makeQuery(id+"F36.opExtrude","CAP_EDGE",EDGE,{"disambiguationData":[OSD([sQuery(id+"F35.wireOp",EDGE,"E87.0")])],"isStart":true});
            var Q72;
            Q72=makeQuery(id+"F36.opExtrude","CAP_EDGE",EDGE,{"disambiguationData":[OSD([sQuery(id+"F35.wireOp",EDGE,"E88.0")])],"isStart":true});
            var Q73;
            Q73=makeQuery(id+"F36.opExtrude","CAP_EDGE",EDGE,{"disambiguationData":[OSD([sQuery(id+"F35.wireOp",EDGE,"E92")])],"isStart":true});
            var Q74;
            Q74=makeQuery(id+"F36.opExtrude","CAP_EDGE",EDGE,{"disambiguationData":[OSD([sQuery(id+"F35.wireOp",EDGE,"E93")])],"isStart":true});
            var Q75;
            Q75=makeQuery(id+"F36.opExtrude","CAP_EDGE",EDGE,{"disambiguationData":[OSD([sQuery(id+"F35.wireOp",EDGE,"E86.0")])],"isStart":true});
            var Q76;
            Q76=makeQuery(id+"F36.opExtrude","SWEPT_EDGE",EDGE,{"disambiguationData":[OSD([sQuery(id+"F35.wireOp",EDGE,"E86.0"),sQuery(id+"F35.wireOp",EDGE,"E87.0")])]});
            var Q77;
            Q77=makeQuery(id+"F36.opExtrude","CAP_EDGE",EDGE,{"disambiguationData":[OSD([sQuery(id+"F35.wireOp",EDGE,"E86.0")])],"isStart":false});
            var Q78;
            Q78=makeQuery(id+"F36.opExtrude","SWEPT_EDGE",EDGE,{"disambiguationData":[OSD([sQuery(id+"F35.wireOp",EDGE,"E86.0"),sQuery(id+"F35.wireOp",EDGE,"E93")])]});
            var Q79;
            Q79=makeQuery(id+"F42.boolean.opBoolean","COPY",EDGE,{"derivedFrom":makeQuery(id+"F42.opExtrude","CAP_EDGE",EDGE,{"disambiguationData":[OSD([sQuery(id+"F41.wireOp",EDGE,"E105")])],"isStart":true})});
            var Q80;
            Q80=makeQuery(id+"F42.boolean.opBoolean","INTERSECT",EDGE,{"derivedFrom":[makeQuery(id+"F36.opExtrude","SWEPT_FACE",FACE,{"disambiguationData":[OSD([sQuery(id+"F35.wireOp",EDGE,"E93")])]}),makeQuery(id+"F42.opExtrude","SWEPT_FACE",FACE,{"disambiguationData":[OSD([sQuery(id+"F41.wireOp",EDGE,"E105")])]})]});
            var Q81;
            Q81=makeQuery(id+"F36.opExtrude","SWEPT_EDGE",EDGE,{"disambiguationData":[OSD([sQuery(id+"F35.wireOp",EDGE,"E89.0"),sQuery(id+"F35.wireOp",EDGE,"E90.0")])]});
            var Q82;
            Q82=makeQuery(id+"F36.opExtrude","CAP_EDGE",EDGE,{"disambiguationData":[OSD([sQuery(id+"F35.wireOp",EDGE,"E90.0")])],"isStart":true});
            var Q83;
            Q83=makeQuery(id+"F36.opExtrude","CAP_EDGE",EDGE,{"disambiguationData":[OSD([sQuery(id+"F35.wireOp",EDGE,"E91.0")])],"isStart":true});
            var Q84;
            Q84=makeQuery(id+"F36.opExtrude","SWEPT_EDGE",EDGE,{"disambiguationData":[OSD([sQuery(id+"F35.wireOp",EDGE,"E90.0"),sQuery(id+"F35.wireOp",EDGE,"E91.0")])]});
            var Q85;
            Q85=makeQuery(id+"F36.opExtrude","CAP_EDGE",EDGE,{"disambiguationData":[OSD([sQuery(id+"F35.wireOp",EDGE,"E90.0")])],"isStart":false});
            var Q86;
            Q86=makeQuery(id+"F36.opExtrude","CAP_EDGE",EDGE,{"disambiguationData":[OSD([sQuery(id+"F35.wireOp",EDGE,"E87.0")])],"isStart":false});
            var Q87;
            Q87=makeQuery(id+"F36.opExtrude","CAP_EDGE",EDGE,{"disambiguationData":[OSD([sQuery(id+"F35.wireOp",EDGE,"E93")])],"isStart":false});
            var Q88;
            Q88=makeQuery(id+"F36.opExtrude","CAP_EDGE",EDGE,{"disambiguationData":[OSD([sQuery(id+"F35.wireOp",EDGE,"E88.0")])],"isStart":false});
            var Q89;
            Q89=makeQuery(id+"F36.opExtrude","CAP_EDGE",EDGE,{"disambiguationData":[OSD([sQuery(id+"F35.wireOp",EDGE,"E89.0")])],"isStart":false});
            var Q90;
            Q90=makeQuery(id+"F36.opExtrude","CAP_EDGE",EDGE,{"disambiguationData":[OSD([sQuery(id+"F35.wireOp",EDGE,"E91.0")])],"isStart":false});
            var Q91;
            Q91=makeQuery(id+"F36.opExtrude","SWEPT_EDGE",EDGE,{"disambiguationData":[OSD([sQuery(id+"F35.wireOp",EDGE,"E91.0"),sQuery(id+"F35.wireOp",EDGE,"E92")])]});
            var Q92;
            Q92=makeQuery(id+"F36.opExtrude","CAP_EDGE",EDGE,{"disambiguationData":[OSD([sQuery(id+"F35.wireOp",EDGE,"E92")])],"isStart":false});
            var Q93;
            Q93=makeQuery(id+"F36.opExtrude","SWEPT_EDGE",EDGE,{"disambiguationData":[OSD([sQuery(id+"F35.wireOp",EDGE,"E92"),sQuery(id+"F35.wireOp",EDGE,"E93")])]});
            var Q94;
            Q94=makeQuery(id+"F38.boolean.opBoolean","COPY",EDGE,{"derivedFrom":makeQuery(id+"F38.opExtrude","CAP_EDGE",EDGE,{"disambiguationData":[OSD([sQuery(id+"F37.wireOp",EDGE,"E95.0")])],"isStart":true})});
            var Q95;
            Q95=makeQuery(id+"F38.boolean.opBoolean","COPY",EDGE,{"derivedFrom":makeQuery(id+"F38.opExtrude","CAP_EDGE",EDGE,{"disambiguationData":[OSD([sQuery(id+"F37.wireOp",EDGE,"E94.0")])],"isStart":true})});
            var Q96;
            Q96=makeQuery(id+"F38.boolean.opBoolean","INTERSECT",EDGE,{"derivedFrom":[makeQuery(id+"F36.opExtrude","CAP_FACE",FACE,{"disambiguationData":[OSD([sQuery(id+"F35.wireOp",EDGE,"E86.0"),sQuery(id+"F35.wireOp",EDGE,"E87.0"),sQuery(id+"F35.wireOp",EDGE,"E88.0"),sQuery(id+"F35.wireOp",EDGE,"E89.0"),sQuery(id+"F35.wireOp",EDGE,"E90.0"),sQuery(id+"F35.wireOp",EDGE,"E91.0"),sQuery(id+"F35.wireOp",EDGE,"E92"),sQuery(id+"F35.wireOp",EDGE,"E93")])],"isStart":false}),makeQuery(id+"F38.opExtrude","SWEPT_FACE",FACE,{"disambiguationData":[OSD([sQuery(id+"F37.wireOp",EDGE,"E94.0")])]})]});
            var Q97;
            Q97=makeQuery(id+"F38.boolean.opBoolean","INTERSECT",EDGE,{"derivedFrom":[makeQuery(id+"F36.opExtrude","CAP_FACE",FACE,{"disambiguationData":[OSD([sQuery(id+"F35.wireOp",EDGE,"E86.0"),sQuery(id+"F35.wireOp",EDGE,"E87.0"),sQuery(id+"F35.wireOp",EDGE,"E88.0"),sQuery(id+"F35.wireOp",EDGE,"E89.0"),sQuery(id+"F35.wireOp",EDGE,"E90.0"),sQuery(id+"F35.wireOp",EDGE,"E91.0"),sQuery(id+"F35.wireOp",EDGE,"E92"),sQuery(id+"F35.wireOp",EDGE,"E93")])],"isStart":false}),makeQuery(id+"F38.opExtrude","SWEPT_FACE",FACE,{"disambiguationData":[OSD([sQuery(id+"F37.wireOp",EDGE,"E95.0")])]})]});
            var Q98;
            {var subQ0=sQuery(id+"F9.wireOp",EDGE,"E33");var subQ1=sQuery(id+"F11.wireOp",EDGE,"E38");var subQ2=sQuery(id+"F0.wireOp",EDGE,"E0");var subQ3=sQuery(id+"F0.wireOp",EDGE,"E1");var subQ4=sQuery(id+"F0.wireOp",EDGE,"E2");var subQ5=sQuery(id+"F0.wireOp",EDGE,"E3");Q98=makeQuery(id+"F19.boolean.opBoolean","MERGE",EDGE,{"derivedFrom":[makeQuery(id+"F15.boolean.opBoolean","SPLIT",EDGE,{"disambiguationData":[TD([makeQuery(id+"F15.opExtrude","SWEPT_FACE",FACE,{"disambiguationData":[OSD([sQuery(id+"F14.wireOp",EDGE,"E42.rect.bottom")])]})])],"derivedFrom":makeQuery(id+"F12.boolean.opBoolean","COPY",EDGE,{"derivedFrom":makeQuery(id+"F12.opExtrude","SWEPT_EDGE",EDGE,{"disambiguationData":[OSD([subQ0,subQ1,sQuery(id+"F11.wireOp",EDGE,"E41")])]})})}),makeQuery(id+"F19.opExtrude","SWEPT_EDGE",EDGE,{"disambiguationData":[OSD([subQ2,subQ3,subQ4,subQ5,subQ1,sQuery(id+"F18.wireOp",EDGE,"E59.0"),sQuery(id+"F18.wireOp",EDGE,"E61.0")])]})]});}
            fillet(context, id + "F43", {"entities" : qUnion([Q0, Q1, Q2, Q3, Q4, Q5, Q6, Q7, Q8, Q9, Q10, Q11, Q12, Q13, Q14, Q15, Q16, Q17, Q18, Q19, Q20, Q21, Q22, Q23, Q24, Q25, Q26, Q27, Q28, Q29, Q30, Q31, Q32, Q33, Q34, Q35, Q36, Q37, Q38, Q39, Q40, Q41, Q42, Q43, Q44, Q45, Q46, Q47, Q48, Q49, Q50, Q51, Q52, Q53, Q54, Q55, Q56, Q57, Q58, Q59, Q60, Q61, Q62, Q63, Q64, Q65, Q66, Q67, Q68, Q69, Q70, Q71, Q72, Q73, Q74, Q75, Q76, Q77, Q78, Q79, Q80, Q81, Q82, Q83, Q84, Q85, Q86, Q87, Q88, Q89, Q90, Q91, Q92, Q93, Q94, Q95, Q96, Q97, Q98]), "radius" : .5 * mm, "tangentPropagation" : true, "allowEdgeOverflow" : false});
        }
        {
            var Q0;
            Q0=qCreatedBy(id+"F2.planeOp",FACE);
            var sketch = newSketch(context, id + "F44", { "sketchPlane" : qUnion([Q0])});
            skCircle(sketch, "E106", {"center": v(0, 0) * mm, "radius": 9.75 * mm});
            skCircle(sketch, "E107", {"center": v(0, 0) * mm, "radius": 8.25 * mm});
            skCircle(sketch, "E108", {"center": v(0, 0) * mm, "radius": 9 * mm, "construction": true});
            skLineSegment(sketch, "E109", {"start": v(0, 0) * mm, "end": v(8.25, 0) * mm, "construction": true});
            skLineSegment(sketch, "E110", {"start": v(8.25, 0) * mm, "end": v(9, 0) * mm, "construction": true});
            skLineSegment(sketch, "E111", {"start": v(9, 0) * mm, "end": v(9.75, 0) * mm, "construction": true});
            skSolve(sketch);
        }
        {
            var Q0;
            Q0 = qSketchRegion(id + "F44", true);
            extrude(context, id + "F45", {"entities" : qUnion([Q0]), "operationType" : NewBodyOperationType.REMOVE, "oppositeDirection" : true, "depth" : 3.5 * mm, "symmetric" : true});
        }
        {
            var Q0;
            Q0=makeQuery(id+"F45.boolean.opBoolean","INTERSECT",EDGE,{"derivedFrom":[makeQuery(id+"F12.boolean.opBoolean","COPY",FACE,{"derivedFrom":makeQuery(id+"F12.opExtrude","SWEPT_FACE",FACE,{"disambiguationData":[OSD([sQuery(id+"F11.wireOp",EDGE,"E36")])]})}),makeQuery(id+"F45.opExtrude","SWEPT_FACE",FACE,{"disambiguationData":[OSD([sQuery(id+"F44.wireOp",EDGE,"E106")])]})]});
            var Q1;
            Q1=makeQuery(id+"F45.boolean.opBoolean","INTERSECT",EDGE,{"derivedFrom":[makeQuery(id+"F12.boolean.opBoolean","COPY",FACE,{"derivedFrom":makeQuery(id+"F12.opExtrude","SWEPT_FACE",FACE,{"disambiguationData":[OSD([sQuery(id+"F11.wireOp",EDGE,"E38")])]})}),makeQuery(id+"F45.opExtrude","SWEPT_FACE",FACE,{"disambiguationData":[OSD([sQuery(id+"F44.wireOp",EDGE,"E106")])]})]});
            var Q2;
            Q2=makeQuery(id+"F45.boolean.opBoolean","INTERSECT",EDGE,{"derivedFrom":[makeQuery(id+"F15.boolean.opBoolean","COPY",FACE,{"derivedFrom":makeQuery(id+"F15.opExtrude","SWEPT_FACE",FACE,{"disambiguationData":[OSD([sQuery(id+"F14.wireOp",EDGE,"E42.rect.left")])]})}),makeQuery(id+"F45.opExtrude","SWEPT_FACE",FACE,{"disambiguationData":[OSD([sQuery(id+"F44.wireOp",EDGE,"E107")])]})]});
            var Q3;
            Q3=makeQuery(id+"F45.boolean.opBoolean","INTERSECT",EDGE,{"derivedFrom":[makeQuery(id+"F15.boolean.opBoolean","COPY",FACE,{"derivedFrom":makeQuery(id+"F15.opExtrude","SWEPT_FACE",FACE,{"disambiguationData":[OSD([sQuery(id+"F14.wireOp",EDGE,"E42.rect.right")])]})}),makeQuery(id+"F45.opExtrude","SWEPT_FACE",FACE,{"disambiguationData":[OSD([sQuery(id+"F44.wireOp",EDGE,"E107")])]})]});
            fillet(context, id + "F46", {"entities" : qUnion([Q0, Q1, Q2, Q3]), "radius" : .5 * mm, "tangentPropagation" : true, "allowEdgeOverflow" : false});
        }
        {
            var Q0;
            Q0=qCreatedBy(makeId("Front.planeOp"),FACE);
            cPlane(context, id + "F47", {"entities" : qUnion([Q0]), "cplaneType" : CPlaneType.OFFSET, "offset" : 20 * mm, "oppositeDirection" : true, "width" : 150 * mm, "height" : 150 * mm});
        }
        {
            var Q0;
            Q0=makeQuery(id+"F8.boolean.opBoolean","SPLIT",BODY,{"disambiguationData":[OD(1.0)],"derivedFrom":makeQuery(id+"F1.opExtrude","SWEPT_BODY",BODY,{"disambiguationData":[OSD([sQuery(id+"F0.wireOp",EDGE,"E0"),sQuery(id+"F0.wireOp",EDGE,"E1"),sQuery(id+"F0.wireOp",EDGE,"E2"),sQuery(id+"F0.wireOp",EDGE,"E3")])]})});
            var Q1;
            Q1=makeQuery(id+"F8.boolean.opBoolean","SPLIT",BODY,{"disambiguationData":[OD(0.0)],"derivedFrom":makeQuery(id+"F1.opExtrude","SWEPT_BODY",BODY,{"disambiguationData":[OSD([sQuery(id+"F0.wireOp",EDGE,"E0"),sQuery(id+"F0.wireOp",EDGE,"E1"),sQuery(id+"F0.wireOp",EDGE,"E2"),sQuery(id+"F0.wireOp",EDGE,"E3")])]})});
            var Q2;
            Q2=qCreatedBy(id+"F47.planeOp",FACE);
            mirror(context, id + "F48", {"entities" : qUnion([Q0, Q1]), "mirrorPlane" : qUnion([Q2])});
        }
        {
            var Q0;
            {var subQ0=sQuery(id+"F0.wireOp",EDGE,"E1");var subQ3=sQuery(id+"F0.wireOp",EDGE,"E3");Q0=makeQuery(id+"F8.boolean.opBoolean","SPLIT",FACE,{"disambiguationData":[TD([makeQuery(id+"F1.opExtrude","SWEPT_FACE",FACE,{"disambiguationData":[OSD([subQ3])]})])],"derivedFrom":makeQuery(id+"F1.opExtrude","SWEPT_FACE",FACE,{"disambiguationData":[OSD([subQ0])]})});}
            var sketch = newSketch(context, id + "F49", { "sketchPlane" : qUnion([Q0])});
            skLineSegment(sketch, "E112", {"start": v(-30.01, 20) * mm, "end": v(-33.5, 20) * mm, "construction": true});
            skLineSegment(sketch, "E113", {"start": v(-25.01, 20) * mm, "end": v(-21.53, 20) * mm, "construction": true});
            skArc(sketch, "E114.0", {"start": v(58, 15.59) * mm, "mid": v(61.53, 20) * mm, "end": v(58, 24.41) * mm, "construction": true});
            skLineSegment(sketch, "E115", {"start": v(-17, 20) * mm, "end": v(20, 20) * mm, "construction": true});
            skLineSegment(sketch, "E116", {"start": v(20, 20) * mm, "end": v(57, 20) * mm, "construction": true});
            skLineSegment(sketch, "E117", {"start": v(57, 20) * mm, "end": v(61.53, 20) * mm, "construction": true});
            skLineSegment(sketch, "E118", {"start": v(61.53, 20) * mm, "end": v(65.01, 20) * mm, "construction": true});
            skText(sketch, "E119", { "text": "Eustathios", "fontName": "OpenSans-BoldItalic.ttf"});
            skLineSegment(sketch, "E120", {"start": v(70.01, 20) * mm, "end": v(73.5, 20) * mm, "construction": true});
            skText(sketch, "E121", { "text": "Eustathios", "fontName": "OpenSans-BoldItalic.ttf"});
            const initialGuessF49  = {"E119": [0.07001, 0.00273, 0, 1, 0.005], "E121": [-0.02501, 0.00273, 0, 1, 0.005]};
            skSetInitialGuess(sketch, initialGuessF49);
            skSolve(sketch);
        }
        {
            var Q0;
            Q0 = qSketchRegion(id + "F49", true);
            extrude(context, id + "F50", {"entities" : qUnion([Q0]), "operationType" : NewBodyOperationType.REMOVE, "oppositeDirection" : true, "depth" : .5 * mm});
        }
    });
